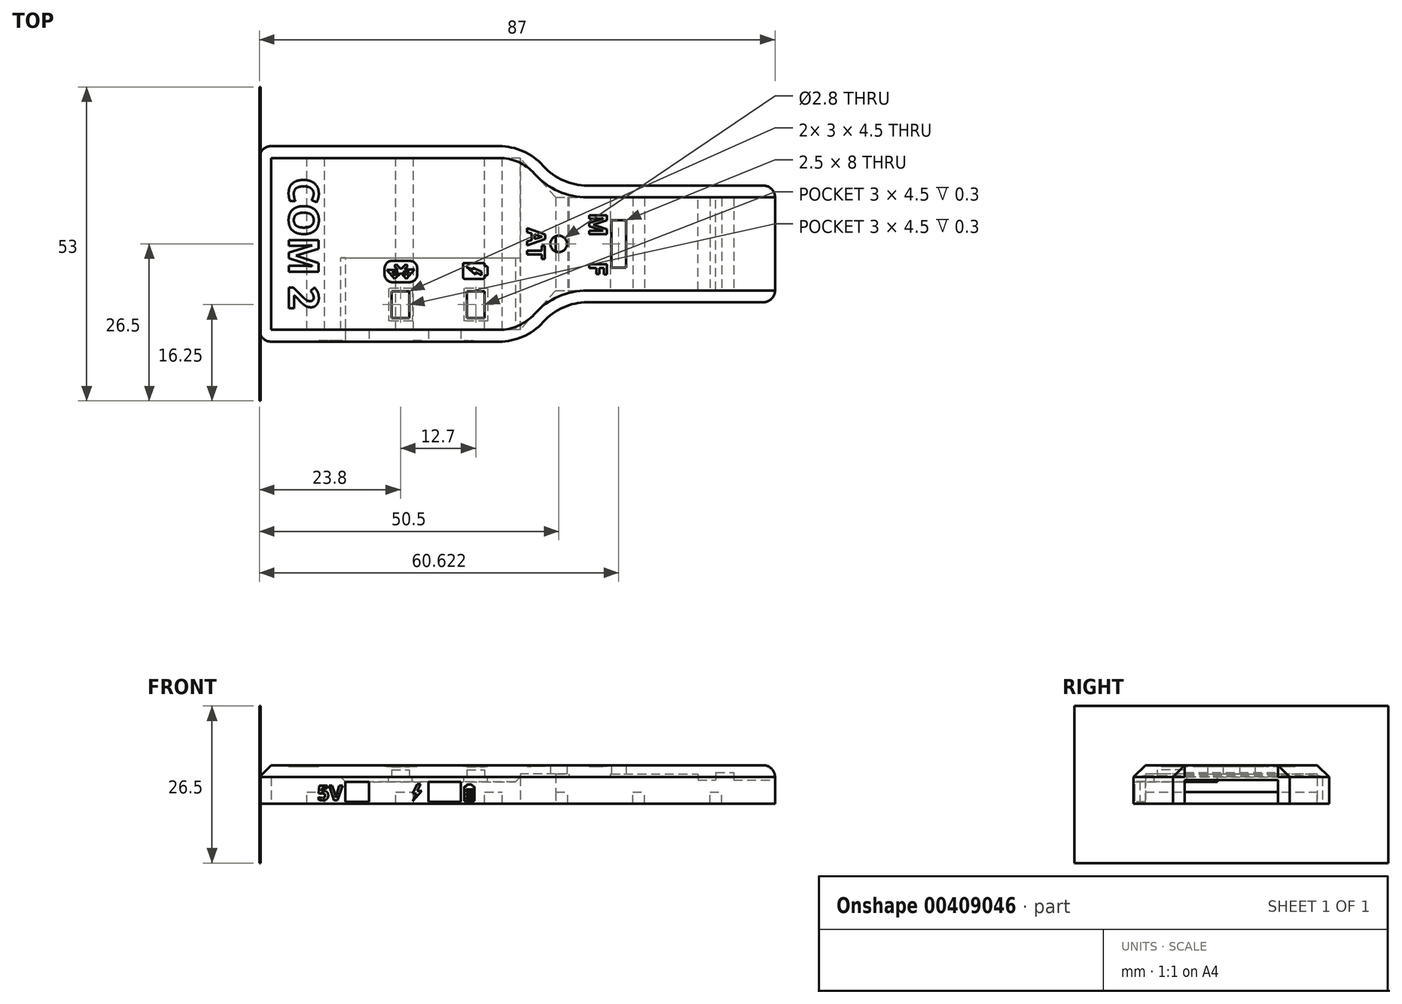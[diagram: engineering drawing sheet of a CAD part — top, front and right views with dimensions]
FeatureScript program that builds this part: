
annotation { "Feature Type Name" : "Feature", "Feature Type Description" : "" }
export const myFeature = defineFeature(function(context is Context, id is Id, definition is map)
    precondition{}
    {
        {
            var Q0;
            Q0=qCreatedBy(makeId("Top.planeOp"),FACE);
            var sketch = newSketch(context, id + "F0", { "sketchPlane" : qUnion([Q0])});
            skLineSegment(sketch, "E0.bottom", {"start": v(0, 14.5) * mm, "end": v(-42, 14.5) * mm});
            skLineSegment(sketch, "E0.top", {"start": v(0, -14.5) * mm, "end": v(-42, -14.5) * mm});
            skLineSegment(sketch, "E0.left", {"start": v(0, 14.5) * mm, "end": v(0, -14.5) * mm});
            skLineSegment(sketch, "E0.right", {"start": v(-42, 14.5) * mm, "end": v(-42, -14.5) * mm});
            skLineSegment(sketch, "E1.bottom", {"start": v(6, 7.85) * mm, "end": v(41, 7.85) * mm});
            skLineSegment(sketch, "E1.top", {"start": v(6, -7.85) * mm, "end": v(41, -7.85) * mm});
            skLineSegment(sketch, "E1.left", {"start": v(6, 7.85) * mm, "end": v(6, -7.85) * mm});
            skLineSegment(sketch, "E1.right", {"start": v(41, 7.85) * mm, "end": v(41, -7.85) * mm});
            skLineSegment(sketch, "E2", {"start": v(6, 7.85) * mm, "end": v(0, 14.5) * mm});
            skLineSegment(sketch, "E3", {"start": v(6, -7.85) * mm, "end": v(0, -14.5) * mm});
            skCircle(sketch, "E4", {"center": v(6.5, 0) * mm, "radius": 1.4 * mm});
            skLineSegment(sketch, "E5.bottom", {"start": v(-29.5, -14.5) * mm, "end": v(-25.5, -14.5) * mm});
            skLineSegment(sketch, "E5.top", {"start": v(-29.5, -17) * mm, "end": v(-25.5, -17) * mm});
            skLineSegment(sketch, "E5.left", {"start": v(-29.5, -14.5) * mm, "end": v(-29.5, -17) * mm});
            skLineSegment(sketch, "E5.right", {"start": v(-25.5, -14.5) * mm, "end": v(-25.5, -17) * mm});
            skLineSegment(sketch, "E6.bottom", {"start": v(-15.5, -14.5) * mm, "end": v(-10, -14.5) * mm});
            skLineSegment(sketch, "E6.top", {"start": v(-15.5, -17) * mm, "end": v(-10, -17) * mm});
            skLineSegment(sketch, "E6.left", {"start": v(-15.5, -14.5) * mm, "end": v(-15.5, -17) * mm});
            skLineSegment(sketch, "E6.right", {"start": v(-10, -14.5) * mm, "end": v(-10, -17) * mm});
            skLineSegment(sketch, "E7.bottom", {"start": v(-21.2, -8.5) * mm, "end": v(-19.2, -8.5) * mm});
            skLineSegment(sketch, "E7.top", {"start": v(-21.2, -12) * mm, "end": v(-19.2, -12) * mm});
            skLineSegment(sketch, "E7.left", {"start": v(-21.2, -8.5) * mm, "end": v(-21.2, -12) * mm});
            skLineSegment(sketch, "E7.right", {"start": v(-19.2, -8.5) * mm, "end": v(-19.2, -12) * mm});
            skLineSegment(sketch, "E8.bottom", {"start": v(-8.5, -8.5) * mm, "end": v(-6.5, -8.5) * mm});
            skLineSegment(sketch, "E8.top", {"start": v(-8.5, -12) * mm, "end": v(-6.5, -12) * mm});
            skLineSegment(sketch, "E8.left", {"start": v(-8.5, -8.5) * mm, "end": v(-8.5, -12) * mm});
            skLineSegment(sketch, "E8.right", {"start": v(-6.5, -8.5) * mm, "end": v(-6.5, -12) * mm});
            skLineSegment(sketch, "E9.bottom", {"start": v(-24.5, -14.5) * mm, "end": v(-30.5, -14.5) * mm});
            skLineSegment(sketch, "E9.top", {"start": v(-24.5, -9.5) * mm, "end": v(-30.5, -9.5) * mm});
            skLineSegment(sketch, "E9.left", {"start": v(-24.5, -14.5) * mm, "end": v(-24.5, -9.5) * mm});
            skLineSegment(sketch, "E9.right", {"start": v(-30.5, -14.5) * mm, "end": v(-30.5, -9.5) * mm});
            skLineSegment(sketch, "E10.bottom", {"start": v(-20, -14.5) * mm, "end": v(-7.5, -14.5) * mm});
            skLineSegment(sketch, "E10.top", {"start": v(-20, -13) * mm, "end": v(-7, -13) * mm});
            skLineSegment(sketch, "E10.left", {"start": v(-20, -14.5) * mm, "end": v(-20, -13) * mm});
            skLineSegment(sketch, "E10.right", {"start": v(-7, -14.5) * mm, "end": v(-7, -13) * mm});
            skLineSegment(sketch, "E11.bottom", {"start": v(8.2, -7.85) * mm, "end": v(15.2, -7.85) * mm});
            skLineSegment(sketch, "E11.top", {"start": v(8.2, 7.85) * mm, "end": v(15.2, 7.85) * mm});
            skLineSegment(sketch, "E11.left", {"start": v(8.2, -7.85) * mm, "end": v(8.2, 7.85) * mm});
            skLineSegment(sketch, "E11.right", {"start": v(15.2, -7.85) * mm, "end": v(15.2, 7.85) * mm});
            skLineSegment(sketch, "E12.bottom", {"start": v(17.87, 4) * mm, "end": v(15.37, 4) * mm});
            skLineSegment(sketch, "E12.top", {"start": v(17.87, -4) * mm, "end": v(15.37, -4) * mm});
            skLineSegment(sketch, "E12.left", {"start": v(17.87, 4) * mm, "end": v(17.87, -4) * mm});
            skLineSegment(sketch, "E12.right", {"start": v(15.37, 4) * mm, "end": v(15.37, -4) * mm});
            skPoint(sketch, "E12.middle", {"position": v(16.62, 0) * mm});
            skLineSegment(sketch, "E13", {"start": v(19, -8) * mm, "end": v(19, 8) * mm});
            skLineSegment(sketch, "E14", {"start": v(30, -7.85) * mm, "end": v(30, 7.85) * mm});
            skLineSegment(sketch, "E15", {"start": v(36, -7.85) * mm, "end": v(36, 7.85) * mm});
            skLineSegment(sketch, "E16", {"start": v(33, -7.85) * mm, "end": v(33, 7.85) * mm});
            skLineSegment(sketch, "E17.0", {"start": v(-9, -12.5) * mm, "end": v(-6, -12.5) * mm});
            skLineSegment(sketch, "E17.1", {"start": v(-9, -8) * mm, "end": v(-9, -12.5) * mm});
            skLineSegment(sketch, "E17.2", {"start": v(-9, -8) * mm, "end": v(-6, -8) * mm});
            skLineSegment(sketch, "E17.3", {"start": v(-6, -8) * mm, "end": v(-6, -12.5) * mm});
            skLineSegment(sketch, "E18.0", {"start": v(-21.7, -12.5) * mm, "end": v(-18.7, -12.5) * mm});
            skLineSegment(sketch, "E18.1", {"start": v(-21.7, -8) * mm, "end": v(-21.7, -12.5) * mm});
            skLineSegment(sketch, "E18.2", {"start": v(-21.7, -8) * mm, "end": v(-18.7, -8) * mm});
            skLineSegment(sketch, "E18.3", {"start": v(-18.7, -8) * mm, "end": v(-18.7, -12.5) * mm});
            skSolve(sketch);
        }
        {
            var Q0;
            Q0=makeQuery(id+"F0.imprint","IMPRINT",FACE,{"disambiguationData":[TD([[makeQuery(id+"F0.imprint","IMPRINT",EDGE,{"derivedFrom":sQuery(id+"F0.wireOp",EDGE,"E0.bottom")}),1.0]])]});
            var Q1;
            Q1=makeQuery(id+"F0.imprint","IMPRINT",FACE,{"disambiguationData":[TD([[makeQuery(id+"F0.imprint","IMPRINT",EDGE,{"derivedFrom":sQuery(id+"F0.wireOp",EDGE,"E9.top")}),1.0]])]});
            var Q2;
            {var subQ0=sQuery(id+"F0.wireOp",EDGE,"E3");Q2=makeQuery(id+"F0.imprint","IMPRINT",FACE,{"disambiguationData":[TD([[makeQuery(id+"F0.imprint","IMPRINT",EDGE,{"derivedFrom":subQ0}),-1.0]])]});}
            var Q3;
            {var subQ0=sQuery(id+"F0.wireOp",EDGE,"E2");Q3=makeQuery(id+"F0.imprint","IMPRINT",FACE,{"disambiguationData":[TD([[makeQuery(id+"F0.imprint","IMPRINT",EDGE,{"derivedFrom":subQ0}),1.0]])]});}
            var Q4;
            Q4=makeQuery(id+"F0.imprint","IMPRINT",FACE,{"disambiguationData":[TD([[makeQuery(id+"F0.imprint","IMPRINT",EDGE,{"derivedFrom":sQuery(id+"F0.wireOp",EDGE,"E10.top")}),-1.0]])]});
            var Q5;
            Q5=makeQuery(id+"F0.imprint","IMPRINT",FACE,{"disambiguationData":[TD([[makeQuery(id+"F0.imprint","IMPRINT",EDGE,{"derivedFrom":sQuery(id+"F0.wireOp",EDGE,"E7.bottom")}),-1.0]])]});
            var Q6;
            Q6=makeQuery(id+"F0.imprint","IMPRINT",FACE,{"disambiguationData":[TD([[makeQuery(id+"F0.imprint","IMPRINT",EDGE,{"derivedFrom":sQuery(id+"F0.wireOp",EDGE,"E7.bottom")}),1.0]])]});
            var Q7;
            Q7=makeQuery(id+"F0.imprint","IMPRINT",FACE,{"disambiguationData":[TD([[makeQuery(id+"F0.imprint","IMPRINT",EDGE,{"derivedFrom":sQuery(id+"F0.wireOp",EDGE,"E8.bottom")}),1.0]])]});
            var Q8;
            Q8=makeQuery(id+"F0.imprint","IMPRINT",FACE,{"disambiguationData":[TD([[makeQuery(id+"F0.imprint","IMPRINT",EDGE,{"derivedFrom":sQuery(id+"F0.wireOp",EDGE,"E8.bottom")}),-1.0]])]});
            extrude(context, id + "F1", {"entities" : qUnion([Q0, Q1, Q2, Q3, Q4, Q5, Q6, Q7, Q8]), "depth" : 4.5 * mm});
        }
        {
            var Q0;
            {var subQ5=sQuery(id+"F0.wireOp",EDGE,"E1.bottom");Q0=makeQuery(id+"F0.imprint","IMPRINT",FACE,{"disambiguationData":[TD([[makeQuery(id+"F0.imprint","IMPRINT",EDGE,{"derivedFrom":subQ5}),-1.0]])]});}
            var Q1;
            {var subQ0=sQuery(id+"F0.wireOp",EDGE,"VPpS5lpm-IVwB-HgLS-dtKc-5THlYFBJEJTK");var subQ1=sQuery(id+"F0.wireOp",EDGE,"E1.left");var subQ2=makeQuery(id+"F0.imprint","INTERSECT",VERTEX,{"disambiguationData":[OD(0.0)],"derivedFrom":[subQ1,subQ0]});Q1=makeQuery(id+"F0.imprint","IMPRINT",FACE,{"disambiguationData":[TD([[makeQuery(id+"F0.imprint","IMPRINT",EDGE,{"disambiguationData":[TD([[subQ2,-1.0]])],"derivedFrom":subQ1}),1.0]])]});}
            var Q2;
            {var subQ0=sQuery(id+"F0.wireOp",EDGE,"E4");var subQ1=sQuery(id+"F0.wireOp",EDGE,"E1.left");var subQ2=makeQuery(id+"F0.imprint","INTERSECT",VERTEX,{"disambiguationData":[OD(0.0)],"derivedFrom":[subQ1,subQ0]});Q2=makeQuery(id+"F0.imprint","IMPRINT",FACE,{"disambiguationData":[TD([[makeQuery(id+"F0.imprint","IMPRINT",EDGE,{"disambiguationData":[TD([[subQ2,-1.0]])],"derivedFrom":subQ1}),1.0]])]});}
            var Q3;
            {var subQ0=sQuery(id+"F0.wireOp",EDGE,"E1.right");Q3=makeQuery(id+"F0.imprint","IMPRINT",FACE,{"disambiguationData":[TD([[makeQuery(id+"F0.imprint","IMPRINT",EDGE,{"derivedFrom":subQ0}),-1.0]])]});}
            var Q4;
            {var subQ1=sQuery(id+"F0.wireOp",EDGE,"E1.left");var subQ4=sQuery(id+"F0.wireOp",EDGE,"VGWTlvGl-73NF-PaTW-xvmp-lA1t04jU08i1");var subQ6=makeQuery(id+"F0.imprint","INTERSECT",VERTEX,{"disambiguationData":[OD(0.0)],"derivedFrom":[subQ1,subQ4]});Q4=makeQuery(id+"F0.imprint","IMPRINT",FACE,{"disambiguationData":[TD([[makeQuery(id+"F0.imprint","IMPRINT",EDGE,{"disambiguationData":[TD([[subQ6,-1.0]])],"derivedFrom":subQ1}),1.0]])]});}
            var Q5;
            {var subQ0=sQuery(id+"F0.wireOp",EDGE,"VGWTlvGl-73NF-PaTW-xvmp-lA1t04jU08i1");var subQ1=sQuery(id+"F0.wireOp",EDGE,"E0.left");var subQ2=makeQuery(id+"F0.imprint","INTERSECT",VERTEX,{"disambiguationData":[OD(0.0)],"derivedFrom":[subQ1,subQ0]});Q5=makeQuery(id+"F0.imprint","IMPRINT",FACE,{"disambiguationData":[TD([[makeQuery(id+"F0.imprint","IMPRINT",EDGE,{"disambiguationData":[TD([[subQ2,-1.0]])],"derivedFrom":subQ1}),-1.0]])]});}
            var Q6;
            {var subQ4=sQuery(id+"F0.wireOp",EDGE,"VGWTlvGl-73NF-PaTW-xvmp-lA1t04jU08i1");var subQ7=sQuery(id+"F0.wireOp",EDGE,"E0.left");var subQ9=makeQuery(id+"F0.imprint","INTERSECT",VERTEX,{"disambiguationData":[OD(0.0)],"derivedFrom":[subQ7,subQ4]});Q6=makeQuery(id+"F0.imprint","IMPRINT",FACE,{"disambiguationData":[TD([[makeQuery(id+"F0.imprint","IMPRINT",EDGE,{"disambiguationData":[TD([[subQ9,-1.0]])],"derivedFrom":subQ7}),1.0]])]});}
            var Q7;
            {var subQ0=sQuery(id+"F0.wireOp",EDGE,"10CGU6lO-faRA-ZIwZ-rcka-2xEhCK4ulN59");var subQ1=sQuery(id+"F0.wireOp",EDGE,"E1.left");var subQ2=makeQuery(id+"F0.imprint","INTERSECT",VERTEX,{"disambiguationData":[OD(0.0)],"derivedFrom":[subQ1,subQ0]});Q7=makeQuery(id+"F0.imprint","IMPRINT",FACE,{"disambiguationData":[TD([[makeQuery(id+"F0.imprint","IMPRINT",EDGE,{"disambiguationData":[TD([[subQ2,-1.0]])],"derivedFrom":subQ1}),-1.0]])]});}
            var Q8;
            {var subQ0=sQuery(id+"F0.wireOp",EDGE,"E4");var subQ1=sQuery(id+"F0.wireOp",EDGE,"E1.left");var subQ2=makeQuery(id+"F0.imprint","INTERSECT",VERTEX,{"disambiguationData":[OD(0.0)],"derivedFrom":[subQ1,subQ0]});Q8=makeQuery(id+"F0.imprint","IMPRINT",FACE,{"disambiguationData":[TD([[makeQuery(id+"F0.imprint","IMPRINT",EDGE,{"disambiguationData":[TD([[subQ2,-1.0]])],"derivedFrom":subQ1}),-1.0]])]});}
            var Q9;
            {var subQ1=sQuery(id+"F0.wireOp",EDGE,"E1.left");var subQ3=sQuery(id+"F0.wireOp",EDGE,"10CGU6lO-faRA-ZIwZ-rcka-2xEhCK4ulN59");var subQ4=makeQuery(id+"F0.imprint","INTERSECT",VERTEX,{"disambiguationData":[OD(0.0)],"derivedFrom":[subQ1,subQ3]});Q9=makeQuery(id+"F0.imprint","IMPRINT",FACE,{"disambiguationData":[TD([[makeQuery(id+"F0.imprint","IMPRINT",EDGE,{"disambiguationData":[TD([[subQ4,1.0]])],"derivedFrom":subQ3}),-1.0]])]});}
            var Q10;
            {var subQ0=sQuery(id+"F0.wireOp",EDGE,"E11.left");var subQ1=sQuery(id+"F0.wireOp",EDGE,"10CGU6lO-faRA-ZIwZ-rcka-2xEhCK4ulN59");var subQ2=makeQuery(id+"F0.imprint","INTERSECT",VERTEX,{"disambiguationData":[OD(0.0)],"derivedFrom":[subQ1,subQ0]});Q10=makeQuery(id+"F0.imprint","IMPRINT",FACE,{"disambiguationData":[TD([[makeQuery(id+"F0.imprint","IMPRINT",EDGE,{"disambiguationData":[TD([[subQ2,1.0]])],"derivedFrom":subQ1}),-1.0]])]});}
            var Q11;
            {var subQ1=sQuery(id+"F0.wireOp",EDGE,"E11.bottom");Q11=makeQuery(id+"F0.imprint","IMPRINT",FACE,{"disambiguationData":[TD([[makeQuery(id+"F0.imprint","IMPRINT",EDGE,{"derivedFrom":subQ1}),1.0]])]});}
            var Q12;
            {var subQ1=sQuery(id+"F0.wireOp",EDGE,"E1.left");var subQ3=sQuery(id+"F0.wireOp",EDGE,"10CGU6lO-faRA-ZIwZ-rcka-2xEhCK4ulN59");var subQ4=makeQuery(id+"F0.imprint","INTERSECT",VERTEX,{"disambiguationData":[OD(1.0)],"derivedFrom":[subQ1,subQ3]});Q12=makeQuery(id+"F0.imprint","IMPRINT",FACE,{"disambiguationData":[TD([[makeQuery(id+"F0.imprint","IMPRINT",EDGE,{"disambiguationData":[TD([[subQ4,-1.0]])],"derivedFrom":subQ3}),-1.0]])]});}
            var Q13;
            {var subQ0=sQuery(id+"F0.wireOp",EDGE,"10CGU6lO-faRA-ZIwZ-rcka-2xEhCK4ulN59");var subQ1=sQuery(id+"F0.wireOp",EDGE,"E1.left");var subQ2=makeQuery(id+"F0.imprint","INTERSECT",VERTEX,{"disambiguationData":[OD(0.0)],"derivedFrom":[subQ1,subQ0]});Q13=makeQuery(id+"F0.imprint","IMPRINT",FACE,{"disambiguationData":[TD([[makeQuery(id+"F0.imprint","IMPRINT",EDGE,{"disambiguationData":[TD([[subQ2,-1.0]])],"derivedFrom":subQ1}),1.0]])]});}
            var Q14;
            {var subQ0=sQuery(id+"F0.wireOp",EDGE,"E11.left");var subQ1=sQuery(id+"F0.wireOp",EDGE,"10CGU6lO-faRA-ZIwZ-rcka-2xEhCK4ulN59");var subQ2=makeQuery(id+"F0.imprint","INTERSECT",VERTEX,{"disambiguationData":[OD(0.0)],"derivedFrom":[subQ1,subQ0]});Q14=makeQuery(id+"F0.imprint","IMPRINT",FACE,{"disambiguationData":[TD([[makeQuery(id+"F0.imprint","IMPRINT",EDGE,{"disambiguationData":[TD([[subQ2,1.0]])],"derivedFrom":subQ1}),1.0]])]});}
            var Q15;
            {var subQ0=sQuery(id+"F0.wireOp",EDGE,"HnFFDSZL-4jIR-ZRKm-03Gk-MsSLVKgGCAKZ");var subQ3=sQuery(id+"F0.wireOp",EDGE,"E11.left");var subQ5=makeQuery(id+"F0.imprint","INTERSECT",VERTEX,{"disambiguationData":[OD(1.0)],"derivedFrom":[subQ0,subQ3]});Q15=makeQuery(id+"F0.imprint","IMPRINT",FACE,{"disambiguationData":[TD([[makeQuery(id+"F0.imprint","IMPRINT",EDGE,{"disambiguationData":[TD([[subQ5,1.0]])],"derivedFrom":subQ3}),1.0]])]});}
            var Q16;
            {var subQ5=sQuery(id+"F0.wireOp",EDGE,"E12.left");Q16=makeQuery(id+"F0.imprint","IMPRINT",FACE,{"disambiguationData":[TD([[makeQuery(id+"F0.imprint","IMPRINT",EDGE,{"derivedFrom":subQ5}),-1.0]])]});}
            var Q17;
            {var subQ5=sQuery(id+"F0.wireOp",EDGE,"E12.right");Q17=makeQuery(id+"F0.imprint","IMPRINT",FACE,{"disambiguationData":[TD([[makeQuery(id+"F0.imprint","IMPRINT",EDGE,{"derivedFrom":subQ5}),1.0]])]});}
            var Q18;
            {var subQ10=sQuery(id+"F0.wireOp",EDGE,"E12.left");Q18=makeQuery(id+"F0.imprint","IMPRINT",FACE,{"disambiguationData":[TD([[makeQuery(id+"F0.imprint","IMPRINT",EDGE,{"derivedFrom":subQ10}),1.0]])]});}
            var Q19;
            {var subQ0=sQuery(id+"F0.wireOp",EDGE,"E13");Q19=makeQuery(id+"F0.imprint","IMPRINT",FACE,{"disambiguationData":[TD([[makeQuery(id+"F0.imprint","IMPRINT",EDGE,{"derivedFrom":subQ0}),-1.0]])]});}
            var Q20;
            {var subQ0=sQuery(id+"F0.wireOp",EDGE,"E14");Q20=makeQuery(id+"F0.imprint","IMPRINT",FACE,{"disambiguationData":[TD([[makeQuery(id+"F0.imprint","IMPRINT",EDGE,{"derivedFrom":subQ0}),-1.0]])]});}
            var Q21;
            {var subQ0=sQuery(id+"F0.wireOp",EDGE,"E15");Q21=makeQuery(id+"F0.imprint","IMPRINT",FACE,{"disambiguationData":[TD([[makeQuery(id+"F0.imprint","IMPRINT",EDGE,{"derivedFrom":subQ0}),1.0]])]});}
            extrude(context, id + "F2", {"entities" : qUnion([Q0, Q1, Q2, Q3, Q4, Q5, Q6, Q7, Q8, Q9, Q10, Q11, Q12, Q13, Q14, Q15, Q16, Q17, Q18, Q19, Q20, Q21]), "depth" : 4.5 * mm});
        }
        {
            var Q0;
            {var subQ0=sQuery(id+"F0.wireOp",EDGE,"VPpS5lpm-IVwB-HgLS-dtKc-5THlYFBJEJTK");var subQ2=sQuery(id+"F0.wireOp",EDGE,"E1.left");var subQ3=makeQuery(id+"F0.imprint","INTERSECT",VERTEX,{"disambiguationData":[OD(0.0)],"derivedFrom":[subQ2,subQ0]});Q0=makeQuery(id+"F0.imprint","IMPRINT",FACE,{"disambiguationData":[TD([[makeQuery(id+"F0.imprint","IMPRINT",EDGE,{"disambiguationData":[TD([[subQ3,-1.0]])],"derivedFrom":subQ2}),-1.0]])]});}
            var Q1;
            {var subQ0=sQuery(id+"F0.wireOp",EDGE,"y9EbTcyz-21YZ-qjv3-pbne-yzflViiAGyzZ");Q1=makeQuery(id+"F0.imprint","IMPRINT",FACE,{"disambiguationData":[TD([[makeQuery(id+"F0.imprint","IMPRINT",EDGE,{"derivedFrom":subQ0}),-1.0]])]});}
            var Q2;
            {var subQ0=sQuery(id+"F0.wireOp",EDGE,"10CGU6lO-faRA-ZIwZ-rcka-2xEhCK4ulN59");var subQ1=sQuery(id+"F0.wireOp",EDGE,"E1.left");var subQ2=makeQuery(id+"F0.imprint","INTERSECT",VERTEX,{"disambiguationData":[OD(0.0)],"derivedFrom":[subQ1,subQ0]});Q2=makeQuery(id+"F0.imprint","IMPRINT",FACE,{"disambiguationData":[TD([[makeQuery(id+"F0.imprint","IMPRINT",EDGE,{"disambiguationData":[TD([[subQ2,-1.0]])],"derivedFrom":subQ1}),-1.0]])]});}
            var Q3;
            {var subQ4=sQuery(id+"F0.wireOp",EDGE,"VGWTlvGl-73NF-PaTW-xvmp-lA1t04jU08i1");var subQ7=sQuery(id+"F0.wireOp",EDGE,"E0.left");var subQ9=makeQuery(id+"F0.imprint","INTERSECT",VERTEX,{"disambiguationData":[OD(0.0)],"derivedFrom":[subQ7,subQ4]});Q3=makeQuery(id+"F0.imprint","IMPRINT",FACE,{"disambiguationData":[TD([[makeQuery(id+"F0.imprint","IMPRINT",EDGE,{"disambiguationData":[TD([[subQ9,-1.0]])],"derivedFrom":subQ7}),1.0]])]});}
            var Q4;
            {var subQ0=sQuery(id+"F0.wireOp",EDGE,"VGWTlvGl-73NF-PaTW-xvmp-lA1t04jU08i1");var subQ1=sQuery(id+"F0.wireOp",EDGE,"E0.left");var subQ2=makeQuery(id+"F0.imprint","INTERSECT",VERTEX,{"disambiguationData":[OD(0.0)],"derivedFrom":[subQ1,subQ0]});Q4=makeQuery(id+"F0.imprint","IMPRINT",FACE,{"disambiguationData":[TD([[makeQuery(id+"F0.imprint","IMPRINT",EDGE,{"disambiguationData":[TD([[subQ2,-1.0]])],"derivedFrom":subQ1}),-1.0]])]});}
            extrude(context, id + "F3", {"entities" : qUnion([Q0, Q1, Q2, Q3, Q4]), "depth" : 4.5 * mm});
        }
        {
            var Q0;
            Q0=makeQuery(id+"F1.opExtrude","SWEPT_BODY",BODY,{"disambiguationData":[OSD([sQuery(id+"F0.wireOp",EDGE,"E0.bottom"),sQuery(id+"F0.wireOp",EDGE,"E0.top"),sQuery(id+"F0.wireOp",EDGE,"E0.right"),sQuery(id+"F0.wireOp",EDGE,"E1.left"),sQuery(id+"F0.wireOp",EDGE,"E2"),sQuery(id+"F0.wireOp",EDGE,"E3"),sQuery(id+"F0.wireOp",EDGE,"E6.bottom"),sQuery(id+"F0.wireOp",EDGE,"E9.bottom"),sQuery(id+"F0.wireOp",EDGE,"VGWTlvGl-73NF-PaTW-xvmp-lA1t04jU08i1")])]});
            var Q1;
            Q1=makeQuery(id+"F2.opExtrude","SWEPT_BODY",BODY,{"disambiguationData":[OSD([sQuery(id+"F0.wireOp",EDGE,"E1.bottom"),sQuery(id+"F0.wireOp",EDGE,"E1.top"),sQuery(id+"F0.wireOp",EDGE,"E1.left"),sQuery(id+"F0.wireOp",EDGE,"E1.right"),sQuery(id+"F0.wireOp",EDGE,"VGWTlvGl-73NF-PaTW-xvmp-lA1t04jU08i1")])]});
            var Q2;
            Q2=makeQuery(id+"F3.opExtrude","SWEPT_BODY",BODY,{"disambiguationData":[OSD([sQuery(id+"F0.wireOp",EDGE,"E1.left"),sQuery(id+"F0.wireOp",EDGE,"E4"),sQuery(id+"F0.wireOp",EDGE,"VGWTlvGl-73NF-PaTW-xvmp-lA1t04jU08i1")])]});
            booleanBodies(context, id + "F4", {"operationType" : BooleanOperationType.UNION, "tools" : qUnion([Q0, Q1, Q2])});
        }
        {
            var Q0;
            {var subQ0=sQuery(id+"F0.wireOp",EDGE,"VGWTlvGl-73NF-PaTW-xvmp-lA1t04jU08i1");var subQ1=sQuery(id+"F0.wireOp",EDGE,"E1.left");Q0=makeQuery(id+"F4.opBoolean","MERGE",FACE,{"derivedFrom":[makeQuery(id+"F1.opExtrude","CAP_FACE",FACE,{"disambiguationData":[OSD([sQuery(id+"F0.wireOp",EDGE,"E0.bottom"),sQuery(id+"F0.wireOp",EDGE,"E0.top"),sQuery(id+"F0.wireOp",EDGE,"E0.right"),subQ1,sQuery(id+"F0.wireOp",EDGE,"E2"),sQuery(id+"F0.wireOp",EDGE,"E3"),sQuery(id+"F0.wireOp",EDGE,"E6.bottom"),sQuery(id+"F0.wireOp",EDGE,"E9.bottom"),subQ0])],"isStart":true}),makeQuery(id+"F2.opExtrude","CAP_FACE",FACE,{"disambiguationData":[OSD([sQuery(id+"F0.wireOp",EDGE,"E1.bottom"),sQuery(id+"F0.wireOp",EDGE,"E1.top"),subQ1,sQuery(id+"F0.wireOp",EDGE,"E1.right"),subQ0])],"isStart":true})]});}
            shell(context, id + "F5", {"entities" : qUnion([Q0]), "thickness" : 2 * mm, "oppositeDirection" : true});
        }
        {
            var Q0;
            {var subQ0=sQuery(id+"F0.wireOp",EDGE,"E4");var subQ1=sQuery(id+"F0.wireOp",EDGE,"E1.left");var subQ2=makeQuery(id+"F0.imprint","INTERSECT",VERTEX,{"disambiguationData":[OD(0.0)],"derivedFrom":[subQ1,subQ0]});Q0=makeQuery(id+"F0.imprint","IMPRINT",FACE,{"disambiguationData":[TD([[makeQuery(id+"F0.imprint","IMPRINT",EDGE,{"disambiguationData":[TD([[subQ2,-1.0]])],"derivedFrom":subQ1}),1.0]])]});}
            var Q1;
            {var subQ0=sQuery(id+"F0.wireOp",EDGE,"E4");var subQ1=sQuery(id+"F0.wireOp",EDGE,"E1.left");var subQ2=makeQuery(id+"F0.imprint","INTERSECT",VERTEX,{"disambiguationData":[OD(0.0)],"derivedFrom":[subQ1,subQ0]});Q1=makeQuery(id+"F0.imprint","IMPRINT",FACE,{"disambiguationData":[TD([[makeQuery(id+"F0.imprint","IMPRINT",EDGE,{"disambiguationData":[TD([[subQ2,-1.0]])],"derivedFrom":subQ1}),-1.0]])]});}
            extrude(context, id + "F6", {"entities" : qUnion([Q0, Q1]), "operationType" : NewBodyOperationType.REMOVE, "depth" : 25 * mm});
        }
        {
            var Q0;
            Q0=makeQuery(id+"F0.imprint","IMPRINT",FACE,{"disambiguationData":[TD([[makeQuery(id+"F0.imprint","IMPRINT",EDGE,{"derivedFrom":sQuery(id+"F0.wireOp",EDGE,"E5.top")}),1.0]])]});
            var Q1;
            Q1=makeQuery(id+"F0.imprint","IMPRINT",FACE,{"disambiguationData":[TD([[makeQuery(id+"F0.imprint","IMPRINT",EDGE,{"derivedFrom":sQuery(id+"F0.wireOp",EDGE,"E6.bottom")}),-1.0]])]});
            var Q2;
            Q2=makeQuery(id+"F0.imprint","IMPRINT",FACE,{"disambiguationData":[TD([[makeQuery(id+"F0.imprint","IMPRINT",EDGE,{"derivedFrom":sQuery(id+"F0.wireOp",EDGE,"E9.top")}),1.0]])]});
            var Q3;
            Q3=makeQuery(id+"F0.imprint","IMPRINT",FACE,{"disambiguationData":[TD([[makeQuery(id+"F0.imprint","IMPRINT",EDGE,{"derivedFrom":sQuery(id+"F0.wireOp",EDGE,"E10.top")}),-1.0]])]});
            var Q4;
            Q4=makeQuery(id+"F0.imprint","IMPRINT",FACE,{"disambiguationData":[TD([[makeQuery(id+"F0.imprint","IMPRINT",EDGE,{"derivedFrom":sQuery(id+"F0.wireOp",EDGE,"E6.top")}),1.0]])]});
            extrude(context, id + "F7", {"entities" : qUnion([Q0, Q1, Q2, Q3, Q4]), "operationType" : NewBodyOperationType.REMOVE, "depth" : 4 * mm});
        }
        {
            var Q0;
            {var subQ0=sQuery(id+"F0.wireOp",EDGE,"HnFFDSZL-4jIR-ZRKm-03Gk-MsSLVKgGCAKZ");var subQ1=sQuery(id+"F0.wireOp",EDGE,"E3");var subQ2=sQuery(id+"F0.wireOp",EDGE,"E1.left");var subQ3=sQuery(id+"F0.wireOp",EDGE,"E1.top");Q0=makeQuery(id+"F4.opBoolean","MERGE",EDGE,{"derivedFrom":[makeQuery(id+"F1.opExtrude","SWEPT_EDGE",EDGE,{"disambiguationData":[OSD([subQ3,subQ2,subQ1,subQ0])]}),makeQuery(id+"F2.opExtrude","SWEPT_EDGE",EDGE,{"disambiguationData":[OSD([subQ3,subQ2,subQ1,subQ0])]})]});}
            var Q1;
            Q1=makeQuery(id+"F1.opExtrude","SWEPT_EDGE",EDGE,{"disambiguationData":[OSD([sQuery(id+"F0.wireOp",EDGE,"E0.top"),sQuery(id+"F0.wireOp",EDGE,"E0.left"),sQuery(id+"F0.wireOp",EDGE,"E3")])]});
            var Q2;
            {var subQ0=sQuery(id+"F0.wireOp",EDGE,"HnFFDSZL-4jIR-ZRKm-03Gk-MsSLVKgGCAKZ");var subQ1=sQuery(id+"F0.wireOp",EDGE,"E2");var subQ2=sQuery(id+"F0.wireOp",EDGE,"E1.left");var subQ3=sQuery(id+"F0.wireOp",EDGE,"E1.bottom");Q2=makeQuery(id+"F4.opBoolean","MERGE",EDGE,{"derivedFrom":[makeQuery(id+"F1.opExtrude","SWEPT_EDGE",EDGE,{"disambiguationData":[OSD([subQ3,subQ2,subQ1,subQ0])]}),makeQuery(id+"F2.opExtrude","SWEPT_EDGE",EDGE,{"disambiguationData":[OSD([subQ3,subQ2,subQ1,subQ0])]})]});}
            var Q3;
            Q3=makeQuery(id+"F1.opExtrude","SWEPT_EDGE",EDGE,{"disambiguationData":[OSD([sQuery(id+"F0.wireOp",EDGE,"E0.bottom"),sQuery(id+"F0.wireOp",EDGE,"E0.left"),sQuery(id+"F0.wireOp",EDGE,"E2")])]});
            fillet(context, id + "F8", {"entities" : qUnion([Q0, Q1, Q2, Q3]), "radius" : 10 * mm, "tangentPropagation" : true, "allowEdgeOverflow" : false});
        }
        {
            var Q0;
            Q0=makeQuery(id+"F5.opShell","OFFSET_FACE",FACE,{"disambiguationData":[OSD([sQuery(id+"F0.wireOp",EDGE,"E1.right")])]});
            extrude(context, id + "F9", {"entities" : qUnion([Q0]), "operationType" : NewBodyOperationType.REMOVE, "oppositeDirection" : true, "depth" : 25 * mm});
        }
        {
            var Q0;
            Q0=makeQuery(id+"F1.opExtrude","SWEPT_EDGE",EDGE,{"disambiguationData":[OSD([sQuery(id+"F0.wireOp",EDGE,"E0.bottom"),sQuery(id+"F0.wireOp",EDGE,"E0.right")])]});
            var Q1;
            Q1=makeQuery(id+"F1.opExtrude","SWEPT_EDGE",EDGE,{"disambiguationData":[OSD([sQuery(id+"F0.wireOp",EDGE,"E0.top"),sQuery(id+"F0.wireOp",EDGE,"E0.right")])]});
            fillet(context, id + "F10", {"entities" : qUnion([Q0, Q1]), "radius" : 2 * mm, "tangentPropagation" : true, "allowEdgeOverflow" : false});
        }
        {
            var Q0;
            {var subQ0=sQuery(id+"F0.wireOp",EDGE,"HnFFDSZL-4jIR-ZRKm-03Gk-MsSLVKgGCAKZ");var subQ7=sQuery(id+"F0.wireOp",EDGE,"E0.left");var subQ8=makeQuery(id+"F0.imprint","INTERSECT",VERTEX,{"disambiguationData":[OD(0.0)],"derivedFrom":[subQ7,subQ0]});Q0=makeQuery(id+"F0.imprint","IMPRINT",FACE,{"disambiguationData":[TD([[makeQuery(id+"F0.imprint","IMPRINT",EDGE,{"disambiguationData":[TD([[subQ8,-1.0]])],"derivedFrom":subQ7}),1.0]])]});}
            var Q1;
            {var subQ0=sQuery(id+"F0.wireOp",EDGE,"10CGU6lO-faRA-ZIwZ-rcka-2xEhCK4ulN59");var subQ1=sQuery(id+"F0.wireOp",EDGE,"E1.left");var subQ2=makeQuery(id+"F0.imprint","INTERSECT",VERTEX,{"disambiguationData":[OD(0.0)],"derivedFrom":[subQ1,subQ0]});Q1=makeQuery(id+"F0.imprint","IMPRINT",FACE,{"disambiguationData":[TD([[makeQuery(id+"F0.imprint","IMPRINT",EDGE,{"disambiguationData":[TD([[subQ2,-1.0]])],"derivedFrom":subQ1}),-1.0]])]});}
            var Q2;
            {var subQ0=sQuery(id+"F0.wireOp",EDGE,"10CGU6lO-faRA-ZIwZ-rcka-2xEhCK4ulN59");var subQ1=sQuery(id+"F0.wireOp",EDGE,"E1.left");var subQ2=makeQuery(id+"F0.imprint","INTERSECT",VERTEX,{"disambiguationData":[OD(0.0)],"derivedFrom":[subQ1,subQ0]});Q2=makeQuery(id+"F0.imprint","IMPRINT",FACE,{"disambiguationData":[TD([[makeQuery(id+"F0.imprint","IMPRINT",EDGE,{"disambiguationData":[TD([[subQ2,-1.0]])],"derivedFrom":subQ1}),1.0]])]});}
            var Q3;
            {var subQ1=sQuery(id+"F0.wireOp",EDGE,"E1.left");var subQ3=sQuery(id+"F0.wireOp",EDGE,"10CGU6lO-faRA-ZIwZ-rcka-2xEhCK4ulN59");var subQ4=makeQuery(id+"F0.imprint","INTERSECT",VERTEX,{"disambiguationData":[OD(0.0)],"derivedFrom":[subQ1,subQ3]});Q3=makeQuery(id+"F0.imprint","IMPRINT",FACE,{"disambiguationData":[TD([[makeQuery(id+"F0.imprint","IMPRINT",EDGE,{"disambiguationData":[TD([[subQ4,1.0]])],"derivedFrom":subQ3}),-1.0]])]});}
            var Q4;
            {var subQ1=sQuery(id+"F0.wireOp",EDGE,"E1.left");var subQ3=sQuery(id+"F0.wireOp",EDGE,"10CGU6lO-faRA-ZIwZ-rcka-2xEhCK4ulN59");var subQ4=makeQuery(id+"F0.imprint","INTERSECT",VERTEX,{"disambiguationData":[OD(1.0)],"derivedFrom":[subQ1,subQ3]});Q4=makeQuery(id+"F0.imprint","IMPRINT",FACE,{"disambiguationData":[TD([[makeQuery(id+"F0.imprint","IMPRINT",EDGE,{"disambiguationData":[TD([[subQ4,-1.0]])],"derivedFrom":subQ3}),-1.0]])]});}
            var Q5;
            {var subQ0=sQuery(id+"F0.wireOp",EDGE,"E11.left");var subQ1=sQuery(id+"F0.wireOp",EDGE,"10CGU6lO-faRA-ZIwZ-rcka-2xEhCK4ulN59");var subQ2=makeQuery(id+"F0.imprint","INTERSECT",VERTEX,{"disambiguationData":[OD(0.0)],"derivedFrom":[subQ1,subQ0]});Q5=makeQuery(id+"F0.imprint","IMPRINT",FACE,{"disambiguationData":[TD([[makeQuery(id+"F0.imprint","IMPRINT",EDGE,{"disambiguationData":[TD([[subQ2,1.0]])],"derivedFrom":subQ1}),1.0]])]});}
            var Q6;
            {var subQ0=sQuery(id+"F0.wireOp",EDGE,"E11.left");var subQ1=sQuery(id+"F0.wireOp",EDGE,"10CGU6lO-faRA-ZIwZ-rcka-2xEhCK4ulN59");var subQ2=makeQuery(id+"F0.imprint","INTERSECT",VERTEX,{"disambiguationData":[OD(0.0)],"derivedFrom":[subQ1,subQ0]});Q6=makeQuery(id+"F0.imprint","IMPRINT",FACE,{"disambiguationData":[TD([[makeQuery(id+"F0.imprint","IMPRINT",EDGE,{"disambiguationData":[TD([[subQ2,1.0]])],"derivedFrom":subQ1}),-1.0]])]});}
            extrude(context, id + "F11", {"entities" : qUnion([Q0, Q1, Q2, Q3, Q4, Q5, Q6]), "operationType" : NewBodyOperationType.REMOVE, "depth" : 5 * mm});
        }
        {
            var Q0;
            {var subQ0=sQuery(id+"F0.wireOp",EDGE,"E11.left");var subQ1=sQuery(id+"F0.wireOp",EDGE,"10CGU6lO-faRA-ZIwZ-rcka-2xEhCK4ulN59");var subQ2=makeQuery(id+"F0.imprint","INTERSECT",VERTEX,{"disambiguationData":[OD(0.0)],"derivedFrom":[subQ1,subQ0]});Q0=makeQuery(id+"F0.imprint","IMPRINT",FACE,{"disambiguationData":[TD([[makeQuery(id+"F0.imprint","IMPRINT",EDGE,{"disambiguationData":[TD([[subQ2,1.0]])],"derivedFrom":subQ1}),1.0]])]});}
            var Q1;
            {var subQ10=sQuery(id+"F0.wireOp",EDGE,"E12.left");Q1=makeQuery(id+"F0.imprint","IMPRINT",FACE,{"disambiguationData":[TD([[makeQuery(id+"F0.imprint","IMPRINT",EDGE,{"derivedFrom":subQ10}),1.0]])]});}
            var Q2;
            {var subQ1=sQuery(id+"F0.wireOp",EDGE,"E11.bottom");Q2=makeQuery(id+"F0.imprint","IMPRINT",FACE,{"disambiguationData":[TD([[makeQuery(id+"F0.imprint","IMPRINT",EDGE,{"derivedFrom":subQ1}),1.0]])]});}
            var Q3;
            {var subQ5=sQuery(id+"F0.wireOp",EDGE,"E12.right");Q3=makeQuery(id+"F0.imprint","IMPRINT",FACE,{"disambiguationData":[TD([[makeQuery(id+"F0.imprint","IMPRINT",EDGE,{"derivedFrom":subQ5}),1.0]])]});}
            var Q4;
            {var subQ0=sQuery(id+"F0.wireOp",EDGE,"HnFFDSZL-4jIR-ZRKm-03Gk-MsSLVKgGCAKZ");var subQ3=sQuery(id+"F0.wireOp",EDGE,"E11.left");var subQ5=makeQuery(id+"F0.imprint","INTERSECT",VERTEX,{"disambiguationData":[OD(1.0)],"derivedFrom":[subQ0,subQ3]});Q4=makeQuery(id+"F0.imprint","IMPRINT",FACE,{"disambiguationData":[TD([[makeQuery(id+"F0.imprint","IMPRINT",EDGE,{"disambiguationData":[TD([[subQ5,1.0]])],"derivedFrom":subQ3}),1.0]])]});}
            var Q5;
            {var subQ0=sQuery(id+"F0.wireOp",EDGE,"HnFFDSZL-4jIR-ZRKm-03Gk-MsSLVKgGCAKZ");var subQ3=sQuery(id+"F0.wireOp",EDGE,"E11.left");var subQ5=makeQuery(id+"F0.imprint","INTERSECT",VERTEX,{"disambiguationData":[OD(0.0)],"derivedFrom":[subQ0,subQ3]});Q5=makeQuery(id+"F0.imprint","IMPRINT",FACE,{"disambiguationData":[TD([[makeQuery(id+"F0.imprint","IMPRINT",EDGE,{"disambiguationData":[TD([[subQ5,-1.0]])],"derivedFrom":subQ3}),1.0]])]});}
            var Q6;
            {var subQ0=sQuery(id+"F0.wireOp",EDGE,"E11.left");var subQ1=sQuery(id+"F0.wireOp",EDGE,"10CGU6lO-faRA-ZIwZ-rcka-2xEhCK4ulN59");var subQ2=makeQuery(id+"F0.imprint","INTERSECT",VERTEX,{"disambiguationData":[OD(0.0)],"derivedFrom":[subQ1,subQ0]});Q6=makeQuery(id+"F0.imprint","IMPRINT",FACE,{"disambiguationData":[TD([[makeQuery(id+"F0.imprint","IMPRINT",EDGE,{"disambiguationData":[TD([[subQ2,1.0]])],"derivedFrom":subQ1}),-1.0]])]});}
            extrude(context, id + "F12", {"entities" : qUnion([Q0, Q1, Q2, Q3, Q4, Q5, Q6]), "operationType" : NewBodyOperationType.REMOVE, "depth" : 5 * mm});
        }
        {
            var Q0;
            {var subQ5=sQuery(id+"F0.wireOp",EDGE,"E12.left");Q0=makeQuery(id+"F0.imprint","IMPRINT",FACE,{"disambiguationData":[TD([[makeQuery(id+"F0.imprint","IMPRINT",EDGE,{"derivedFrom":subQ5}),-1.0]])]});}
            extrude(context, id + "F13", {"entities" : qUnion([Q0]), "operationType" : NewBodyOperationType.REMOVE, "depth" : 25 * mm});
        }
        {
            var Q0;
            {var subQ0=sQuery(id+"F0.wireOp",EDGE,"E15");Q0=makeQuery(id+"F0.imprint","IMPRINT",FACE,{"disambiguationData":[TD([[makeQuery(id+"F0.imprint","IMPRINT",EDGE,{"derivedFrom":subQ0}),1.0]])]});}
            var Q1;
            {var subQ0=sQuery(id+"F0.wireOp",EDGE,"E13");Q1=makeQuery(id+"F0.imprint","IMPRINT",FACE,{"disambiguationData":[TD([[makeQuery(id+"F0.imprint","IMPRINT",EDGE,{"derivedFrom":subQ0}),-1.0]])]});}
            extrude(context, id + "F14", {"entities" : qUnion([Q0, Q1]), "operationType" : NewBodyOperationType.REMOVE, "depth" : 5 * mm});
        }
        {
            var Q0;
            {var subQ0=sQuery(id+"F0.wireOp",EDGE,"HnFFDSZL-4jIR-ZRKm-03Gk-MsSLVKgGCAKZ");Q0=makeQuery(id+"F4.opBoolean","MERGE",FACE,{"derivedFrom":[makeQuery(id+"F1.opExtrude","CAP_FACE",FACE,{"disambiguationData":[OSD([sQuery(id+"F0.wireOp",EDGE,"E0.bottom"),sQuery(id+"F0.wireOp",EDGE,"E0.top"),sQuery(id+"F0.wireOp",EDGE,"E0.right"),sQuery(id+"F0.wireOp",EDGE,"E2"),sQuery(id+"F0.wireOp",EDGE,"E3"),sQuery(id+"F0.wireOp",EDGE,"E9.bottom"),sQuery(id+"F0.wireOp",EDGE,"E10.bottom"),subQ0])],"isStart":false}),makeQuery(id+"F2.opExtrude","CAP_FACE",FACE,{"disambiguationData":[OSD([sQuery(id+"F0.wireOp",EDGE,"E1.bottom"),sQuery(id+"F0.wireOp",EDGE,"E1.top"),sQuery(id+"F0.wireOp",EDGE,"E1.right"),subQ0,sQuery(id+"F0.wireOp",EDGE,"E11.bottom"),sQuery(id+"F0.wireOp",EDGE,"E11.top")])],"isStart":false})]});}
            var sketch = newSketch(context, id + "F15", { "sketchPlane" : qUnion([Q0])});
            skPoint(sketch, "E19.middle", {"position": v(-19.64, -4.61) * mm});
            skLineSegment(sketch, "E20", {"start": v(-18.72, -4.71) * mm, "end": v(-19.8, -4.73) * mm});
            skLineSegment(sketch, "E21", {"start": v(-19.8, -4.73) * mm, "end": v(-19.22, -5.28) * mm});
            skLineSegment(sketch, "E22", {"start": v(-19.22, -5.28) * mm, "end": v(-18.72, -4.71) * mm});
            skLineSegment(sketch, "E23", {"start": v(-20.54, -4.76) * mm, "end": v(-21.66, -4.76) * mm});
            skLineSegment(sketch, "E24", {"start": v(-21.66, -4.76) * mm, "end": v(-21.13, -5.31) * mm});
            skLineSegment(sketch, "E25", {"start": v(-21.13, -5.31) * mm, "end": v(-20.54, -4.76) * mm});
            skLineSegment(sketch, "E26", {"start": v(-20.12, -4.91) * mm, "end": v(-21.19, -5.94) * mm});
            skLineSegment(sketch, "E27", {"start": v(-21.19, -5.94) * mm, "end": v(-22.52, -4.36) * mm});
            skLineSegment(sketch, "E28", {"start": v(-22.52, -4.36) * mm, "end": v(-20.6, -4.37) * mm});
            skLineSegment(sketch, "E29", {"start": v(-20.6, -4.37) * mm, "end": v(-21.24, -3.74) * mm});
            skLineSegment(sketch, "E30", {"start": v(-21.24, -3.74) * mm, "end": v(-20.95, -3.45) * mm});
            skLineSegment(sketch, "E31", {"start": v(-20.95, -3.45) * mm, "end": v(-20.1, -4.28) * mm});
            skLineSegment(sketch, "E32", {"start": v(-20.1, -4.28) * mm, "end": v(-19.28, -3.45) * mm});
            skLineSegment(sketch, "E33", {"start": v(-19.28, -3.45) * mm, "end": v(-18.97, -3.75) * mm});
            skLineSegment(sketch, "E34", {"start": v(-18.97, -3.75) * mm, "end": v(-19.56, -4.34) * mm});
            skLineSegment(sketch, "E35", {"start": v(-19.56, -4.34) * mm, "end": v(-17.84, -4.33) * mm});
            skLineSegment(sketch, "E36", {"start": v(-17.84, -4.33) * mm, "end": v(-19.2, -5.89) * mm});
            skLineSegment(sketch, "E37", {"start": v(-19.2, -5.89) * mm, "end": v(-20.12, -4.91) * mm});
            skText(sketch, "E38", { "text": "M    F", "fontName": "OpenSans-Bold.ttf"});
            skText(sketch, "E39", { "text": "AT", "fontName": "OpenSans-Bold.ttf"});
            skText(sketch, "E40", { "text": "COM 2", "fontName": "OpenSans-Bold.ttf"});
            skLineSegment(sketch, "E41.bottom", {"start": v(-6.24, -3.21) * mm, "end": v(-9.4, -3.21) * mm});
            skLineSegment(sketch, "E41.top", {"start": v(-6.24, -5.9) * mm, "end": v(-9.4, -5.9) * mm});
            skLineSegment(sketch, "E41.left", {"start": v(-6, -3.44) * mm, "end": v(-6, -5.66) * mm});
            skLineSegment(sketch, "E41.right", {"start": v(-9.63, -3.44) * mm, "end": v(-9.63, -5.66) * mm});
            skPoint(sketch, "E42.visualSharp", {"position": v(-6, -3.21) * mm});
            skArc(sketch, "E42.filletArc", {"start": v(-6, -3.44) * mm, "mid": v(-6.07, -3.28) * mm, "end": v(-6.24, -3.21) * mm});
            skPoint(sketch, "E43.visualSharp", {"position": v(-6, -5.9) * mm});
            skArc(sketch, "E43.filletArc", {"start": v(-6.24, -5.9) * mm, "mid": v(-6.07, -5.83) * mm, "end": v(-6, -5.66) * mm});
            skPoint(sketch, "E44.visualSharp", {"position": v(-9.63, -3.21) * mm});
            skArc(sketch, "E44.filletArc", {"start": v(-9.4, -3.21) * mm, "mid": v(-9.56, -3.28) * mm, "end": v(-9.63, -3.44) * mm});
            skPoint(sketch, "E45.visualSharp", {"position": v(-9.63, -5.9) * mm});
            skArc(sketch, "E45.filletArc", {"start": v(-9.63, -5.66) * mm, "mid": v(-9.56, -5.83) * mm, "end": v(-9.4, -5.9) * mm});
            skLineSegment(sketch, "E46.bottom", {"start": v(-6, -3.76) * mm, "end": v(-5.74, -3.76) * mm});
            skLineSegment(sketch, "E46.top", {"start": v(-6, -5.35) * mm, "end": v(-5.74, -5.35) * mm});
            skLineSegment(sketch, "E46.left", {"start": v(-6, -3.76) * mm, "end": v(-6, -5.35) * mm});
            skLineSegment(sketch, "E46.right", {"start": v(-5.5, -4) * mm, "end": v(-5.5, -5.11) * mm});
            skPoint(sketch, "E47.visualSharp", {"position": v(-5.5, -3.76) * mm});
            skArc(sketch, "E47.filletArc", {"start": v(-5.5, -4) * mm, "mid": v(-5.57, -3.83) * mm, "end": v(-5.74, -3.76) * mm});
            skPoint(sketch, "E48.visualSharp", {"position": v(-5.5, -5.35) * mm});
            skArc(sketch, "E48.filletArc", {"start": v(-5.74, -5.35) * mm, "mid": v(-5.57, -5.28) * mm, "end": v(-5.5, -5.11) * mm});
            skLineSegment(sketch, "E49", {"start": v(-6.53, -4.71) * mm, "end": v(-7.98, -4) * mm});
            skLineSegment(sketch, "E50", {"start": v(-7.98, -4) * mm, "end": v(-7.98, -4.4) * mm});
            skLineSegment(sketch, "E51", {"start": v(-7.98, -4.4) * mm, "end": v(-9.07, -3.9) * mm});
            skLineSegment(sketch, "E52", {"start": v(-9.07, -3.9) * mm, "end": v(-7.5, -5.2) * mm});
            skLineSegment(sketch, "E53", {"start": v(-7.5, -5.2) * mm, "end": v(-7.5, -4.76) * mm});
            skLineSegment(sketch, "E54", {"start": v(-7.5, -4.76) * mm, "end": v(-6.53, -5.25) * mm});
            skLineSegment(sketch, "E55", {"start": v(-6.53, -5.25) * mm, "end": v(-6.53, -4.71) * mm});
            skLineSegment(sketch, "E56.bottom", {"start": v(-21.54, -6.47) * mm, "end": v(-18.7, -6.47) * mm});
            skLineSegment(sketch, "E56.top", {"start": v(-21.54, -2.84) * mm, "end": v(-18.7, -2.84) * mm});
            skLineSegment(sketch, "E56.left", {"start": v(-22.89, -5.12) * mm, "end": v(-22.89, -4.19) * mm});
            skLineSegment(sketch, "E56.right", {"start": v(-17.35, -5.12) * mm, "end": v(-17.35, -4.19) * mm});
            skPoint(sketch, "E56.middle", {"position": v(-20.12, -4.65) * mm});
            skPoint(sketch, "E57.visualSharp", {"position": v(-17.35, -2.84) * mm});
            skArc(sketch, "E57.filletArc", {"start": v(-17.35, -4.19) * mm, "mid": v(-17.75, -3.23) * mm, "end": v(-18.7, -2.84) * mm});
            skPoint(sketch, "E58.visualSharp", {"position": v(-17.35, -6.47) * mm});
            skArc(sketch, "E58.filletArc", {"start": v(-18.7, -6.47) * mm, "mid": v(-17.75, -6.07) * mm, "end": v(-17.35, -5.12) * mm});
            skPoint(sketch, "E59.visualSharp", {"position": v(-22.89, -6.47) * mm});
            skArc(sketch, "E59.filletArc", {"start": v(-22.89, -5.12) * mm, "mid": v(-22.5, -6.07) * mm, "end": v(-21.54, -6.47) * mm});
            skPoint(sketch, "E60.visualSharp", {"position": v(-22.89, -2.84) * mm});
            skArc(sketch, "E60.filletArc", {"start": v(-21.54, -2.84) * mm, "mid": v(-22.5, -3.23) * mm, "end": v(-22.89, -4.19) * mm});
            const initialGuessF15  = {"E38": [0.01167, 0.0052, 0, -1, 0.003], "E39": [0.0012, 0.00264, 0, -1, 0.003], "E40": [-0.039, 0.0112, 0, -1, 0.005]};
            skSetInitialGuess(sketch, initialGuessF15);
            skSolve(sketch);
        }
        {
            var Q0;
            {var subQ5=sQuery(id+"F15.wireOp",EDGE,"E19.right");Q0=makeQuery(id+"F15.imprint","IMPRINT",FACE,{"disambiguationData":[TD([[makeQuery(id+"F15.imprint","IMPRINT",EDGE,{"derivedFrom":subQ5}),1.0]])]});}
            var Q1;
            {var subQ0=sQuery(id+"F15.wireOp",EDGE,"E19.top");var subQ1=sQuery(id+"F15.wireOp",EDGE,"FoTjqakA-3Q0D-e8Zx-aRf2-kQgUUboiUMlV");var subQ2=makeQuery(id+"F15.imprint","INTERSECT",VERTEX,{"derivedFrom":[subQ1,subQ0]});Q1=makeQuery(id+"F15.imprint","IMPRINT",FACE,{"disambiguationData":[TD([[makeQuery(id+"F15.imprint","IMPRINT",EDGE,{"disambiguationData":[TD([[subQ2,1.0]])],"derivedFrom":subQ1}),-1.0]])]});}
            var Q2;
            {var subQ5=sQuery(id+"F15.wireOp",EDGE,"E19.left");Q2=makeQuery(id+"F15.imprint","IMPRINT",FACE,{"disambiguationData":[TD([[makeQuery(id+"F15.imprint","IMPRINT",EDGE,{"derivedFrom":subQ5}),-1.0]])]});}
            var Q3;
            {var subQ0=sQuery(id+"F15.wireOp",EDGE,"1H3nl5ng-9DyI-yJWU-6AWz-InJrUK3OAsY4");Q3=makeQuery(id+"F15.imprint","IMPRINT",FACE,{"disambiguationData":[TD([[makeQuery(id+"F15.imprint","IMPRINT",EDGE,{"derivedFrom":subQ0}),-1.0]])]});}
            var Q4;
            Q4=makeQuery(id+"F15.imprint","IMPRINT",FACE,{"disambiguationData":[TD([[makeQuery(id+"F15.imprint","IMPRINT",EDGE,{"derivedFrom":sQuery(id+"F15.wireOp",EDGE,"tPRg0zax-F67y-5KnP-cIeF-lg8p1GO7OnOK")}),-1.0]])]});
            var Q5;
            Q5=makeQuery(id+"F15.imprint","IMPRINT",FACE,{"disambiguationData":[TD([[makeQuery(id+"F15.imprint","IMPRINT",EDGE,{"derivedFrom":sQuery(id+"F15.wireOp",EDGE,"E39.sketch_text.stroke-0")}),-1.0]])]});
            var Q6;
            Q6=makeQuery(id+"F15.imprint","IMPRINT",FACE,{"disambiguationData":[TD([[makeQuery(id+"F15.imprint","IMPRINT",EDGE,{"derivedFrom":sQuery(id+"F15.wireOp",EDGE,"E39.sketch_text.stroke-13")}),-1.0]])]});
            var Q7;
            Q7=makeQuery(id+"F15.imprint","IMPRINT",FACE,{"disambiguationData":[TD([[makeQuery(id+"F15.imprint","IMPRINT",EDGE,{"derivedFrom":sQuery(id+"F15.wireOp",EDGE,"E38.sketch_text.stroke-18")}),-1.0]])]});
            var Q8;
            Q8=makeQuery(id+"F15.imprint","IMPRINT",FACE,{"disambiguationData":[TD([[makeQuery(id+"F15.imprint","IMPRINT",EDGE,{"derivedFrom":sQuery(id+"F15.wireOp",EDGE,"E38.sketch_text.stroke-0")}),-1.0]])]});
            var Q9;
            Q9=makeQuery(id+"F15.imprint","IMPRINT",FACE,{"disambiguationData":[TD([[makeQuery(id+"F15.imprint","IMPRINT",EDGE,{"derivedFrom":sQuery(id+"F15.wireOp",EDGE,"E38.sketch_text.stroke-19")}),-1.0]])]});
            var Q10;
            Q10=makeQuery(id+"F15.imprint","IMPRINT",FACE,{"disambiguationData":[TD([[makeQuery(id+"F15.imprint","IMPRINT",EDGE,{"derivedFrom":sQuery(id+"F15.wireOp",EDGE,"E46.bottom")}),-1.0]])]});
            var Q11;
            Q11=makeQuery(id+"F15.imprint","IMPRINT",FACE,{"disambiguationData":[TD([[makeQuery(id+"F15.imprint","IMPRINT",EDGE,{"derivedFrom":sQuery(id+"F15.wireOp",EDGE,"E41.bottom")}),1.0]])]});
            var Q12;
            Q12=makeQuery(id+"F15.imprint","IMPRINT",FACE,{"disambiguationData":[TD([[makeQuery(id+"F15.imprint","IMPRINT",EDGE,{"derivedFrom":sQuery(id+"F15.wireOp",EDGE,"E23")}),1.0]])]});
            var Q13;
            Q13=makeQuery(id+"F15.imprint","IMPRINT",FACE,{"disambiguationData":[TD([[makeQuery(id+"F15.imprint","IMPRINT",EDGE,{"derivedFrom":sQuery(id+"F15.wireOp",EDGE,"E20")}),1.0]])]});
            var Q14;
            Q14=makeQuery(id+"F15.imprint","IMPRINT",FACE,{"disambiguationData":[TD([[makeQuery(id+"F15.imprint","IMPRINT",EDGE,{"derivedFrom":sQuery(id+"F15.wireOp",EDGE,"E26")}),1.0]])]});
            extrude(context, id + "F16", {"entities" : qUnion([Q0, Q1, Q2, Q3, Q4, Q5, Q6, Q7, Q8, Q9, Q10, Q11, Q12, Q13, Q14]), "operationType" : NewBodyOperationType.REMOVE, "oppositeDirection" : true, "depth" : 0.2 * mm});
        }
        {
            var Q0;
            Q0=makeQuery(id+"F2.opExtrude","CAP_EDGE",EDGE,{"disambiguationData":[OSD([sQuery(id+"F0.wireOp",EDGE,"E1.right")])],"isStart":false});
            var Q1;
            Q1=makeQuery(id+"F2.opExtrude","SWEPT_EDGE",EDGE,{"disambiguationData":[OSD([sQuery(id+"F0.wireOp",EDGE,"E1.top"),sQuery(id+"F0.wireOp",EDGE,"E1.right")])]});
            var Q2;
            Q2=makeQuery(id+"F2.opExtrude","SWEPT_EDGE",EDGE,{"disambiguationData":[OSD([sQuery(id+"F0.wireOp",EDGE,"E1.bottom"),sQuery(id+"F0.wireOp",EDGE,"E1.right")])]});
            fillet(context, id + "F17", {"entities" : qUnion([Q0, Q1, Q2]), "radius" : 2 * mm, "tangentPropagation" : true, "allowEdgeOverflow" : false});
        }
        {
            var Q0;
            Q0=makeQuery(id+"F2.opExtrude","CAP_EDGE",EDGE,{"disambiguationData":[OSD([sQuery(id+"F0.wireOp",EDGE,"E1.top"),sQuery(id+"F0.wireOp",EDGE,"E11.bottom")])],"isStart":false});
            var Q1;
            Q1=makeQuery(id+"F2.opExtrude","CAP_EDGE",EDGE,{"disambiguationData":[OSD([sQuery(id+"F0.wireOp",EDGE,"E1.bottom"),sQuery(id+"F0.wireOp",EDGE,"E11.top")])],"isStart":false});
            chamfer(context, id + "F18", {"entities" : qUnion([Q0, Q1]), "width" : 2 * mm, "tangentPropagation" : true});
        }
        {
            var Q0;
            Q0=makeQuery(id+"F0.imprint","IMPRINT",FACE,{"disambiguationData":[TD([[makeQuery(id+"F0.imprint","IMPRINT",EDGE,{"derivedFrom":sQuery(id+"F0.wireOp",EDGE,"E7.bottom")}),-1.0]])]});
            var Q1;
            Q1=makeQuery(id+"F0.imprint","IMPRINT",FACE,{"disambiguationData":[TD([[makeQuery(id+"F0.imprint","IMPRINT",EDGE,{"derivedFrom":sQuery(id+"F0.wireOp",EDGE,"E7.bottom")}),1.0]])]});
            var Q2;
            Q2=makeQuery(id+"F0.imprint","IMPRINT",FACE,{"disambiguationData":[TD([[makeQuery(id+"F0.imprint","IMPRINT",EDGE,{"derivedFrom":sQuery(id+"F0.wireOp",EDGE,"E8.bottom")}),1.0]])]});
            var Q3;
            Q3=makeQuery(id+"F0.imprint","IMPRINT",FACE,{"disambiguationData":[TD([[makeQuery(id+"F0.imprint","IMPRINT",EDGE,{"derivedFrom":sQuery(id+"F0.wireOp",EDGE,"E8.bottom")}),-1.0]])]});
            extrude(context, id + "F19", {"entities" : qUnion([Q0, Q1, Q2, Q3]), "operationType" : NewBodyOperationType.REMOVE, "endBound" : BoundingType.THROUGH_ALL, "depth" : 25 * mm});
        }
        {
            var Q0;
            Q0=makeQuery(id+"F0.imprint","IMPRINT",FACE,{"disambiguationData":[TD([[makeQuery(id+"F0.imprint","IMPRINT",EDGE,{"derivedFrom":sQuery(id+"F0.wireOp",EDGE,"E7.bottom")}),1.0]])]});
            var Q1;
            Q1=makeQuery(id+"F0.imprint","IMPRINT",FACE,{"disambiguationData":[TD([[makeQuery(id+"F0.imprint","IMPRINT",EDGE,{"derivedFrom":sQuery(id+"F0.wireOp",EDGE,"E7.bottom")}),-1.0]])]});
            var Q2;
            Q2=makeQuery(id+"F0.imprint","IMPRINT",FACE,{"disambiguationData":[TD([[makeQuery(id+"F0.imprint","IMPRINT",EDGE,{"derivedFrom":sQuery(id+"F0.wireOp",EDGE,"E8.bottom")}),1.0]])]});
            var Q3;
            Q3=makeQuery(id+"F0.imprint","IMPRINT",FACE,{"disambiguationData":[TD([[makeQuery(id+"F0.imprint","IMPRINT",EDGE,{"derivedFrom":sQuery(id+"F0.wireOp",EDGE,"E8.bottom")}),-1.0]])]});
            extrude(context, id + "F20", {"entities" : qUnion([Q0, Q1, Q2, Q3]), "operationType" : NewBodyOperationType.ADD, "depth" : 6.2 * mm});
        }
        {
            var Q0;
            Q0=makeQuery(id+"F0.imprint","IMPRINT",FACE,{"disambiguationData":[TD([[makeQuery(id+"F0.imprint","IMPRINT",EDGE,{"derivedFrom":sQuery(id+"F0.wireOp",EDGE,"E7.bottom")}),1.0]])]});
            var Q1;
            Q1=makeQuery(id+"F0.imprint","IMPRINT",FACE,{"disambiguationData":[TD([[makeQuery(id+"F0.imprint","IMPRINT",EDGE,{"derivedFrom":sQuery(id+"F0.wireOp",EDGE,"E8.bottom")}),1.0]])]});
            var Q2;
            Q2=makeQuery(id+"F0.imprint","IMPRINT",FACE,{"disambiguationData":[TD([[makeQuery(id+"F0.imprint","IMPRINT",EDGE,{"derivedFrom":sQuery(id+"F0.wireOp",EDGE,"E7.bottom")}),-1.0]])]});
            var Q3;
            Q3=makeQuery(id+"F0.imprint","IMPRINT",FACE,{"disambiguationData":[TD([[makeQuery(id+"F0.imprint","IMPRINT",EDGE,{"derivedFrom":sQuery(id+"F0.wireOp",EDGE,"E8.bottom")}),-1.0]])]});
            extrude(context, id + "F21", {"entities" : qUnion([Q0, Q1, Q2, Q3]), "operationType" : NewBodyOperationType.REMOVE, "depth" : 5.7 * mm});
        }
        {
            var Q0;
            Q0=makeQuery(id+"F1.opExtrude","SWEPT_FACE",FACE,{"disambiguationData":[OSD([sQuery(id+"F0.wireOp",EDGE,"E0.top"),sQuery(id+"F0.wireOp",EDGE,"E9.bottom"),sQuery(id+"F0.wireOp",EDGE,"E10.bottom")])]});
            var sketch = newSketch(context, id + "F22", { "sketchPlane" : qUnion([Q0])});
            skText(sketch, "E61", { "text": "5V", "fontName": "OpenSans-Bold.ttf"});
            skLineSegment(sketch, "E62.bottom", {"start": v(-9.26, 2.92) * mm, "end": v(-7.89, 2.92) * mm});
            skLineSegment(sketch, "E62.top", {"start": v(-9.26, 0.45) * mm, "end": v(-7.89, 0.45) * mm});
            skLineSegment(sketch, "E62.left", {"start": v(-9.46, 2.72) * mm, "end": v(-9.46, 0.65) * mm});
            skLineSegment(sketch, "E62.right", {"start": v(-7.69, 2.72) * mm, "end": v(-7.69, 0.65) * mm});
            skLineSegment(sketch, "E63.bottom", {"start": v(-8.88, 3.22) * mm, "end": v(-8.25, 3.22) * mm});
            skLineSegment(sketch, "E63.top", {"start": v(-9.08, 3.23) * mm, "end": v(-8.05, 3.23) * mm});
            skLineSegment(sketch, "E63.left", {"start": v(-9.08, 3.02) * mm, "end": v(-9.08, 2.92) * mm});
            skLineSegment(sketch, "E63.right", {"start": v(-8.05, 3.02) * mm, "end": v(-8.05, 2.92) * mm});
            skPoint(sketch, "E64.visualSharp", {"position": v(-9.46, 3.23) * mm});
            skArc(sketch, "E64.filletArc", {"start": v(-9.26, 2.92) * mm, "mid": v(-9.4, 2.86) * mm, "end": v(-9.46, 2.72) * mm});
            skPoint(sketch, "E65.visualSharp", {"position": v(-7.69, 3.23) * mm});
            skArc(sketch, "E65.filletArc", {"start": v(-7.69, 2.72) * mm, "mid": v(-7.75, 2.86) * mm, "end": v(-7.89, 2.92) * mm});
            skPoint(sketch, "E66.visualSharp", {"position": v(-9.46, 0.76) * mm});
            skArc(sketch, "E66.filletArc", {"start": v(-9.46, 0.65) * mm, "mid": v(-9.4, 0.5) * mm, "end": v(-9.26, 0.45) * mm});
            skPoint(sketch, "E67.visualSharp", {"position": v(-7.69, 0.76) * mm});
            skArc(sketch, "E67.filletArc", {"start": v(-7.89, 0.45) * mm, "mid": v(-7.75, 0.5) * mm, "end": v(-7.69, 0.65) * mm});
            skPoint(sketch, "E68.visualSharp", {"position": v(-9.08, 3.53) * mm});
            skArc(sketch, "E68.filletArc", {"start": v(-8.88, 3.22) * mm, "mid": v(-9.02, 3.16) * mm, "end": v(-9.08, 3.02) * mm});
            skPoint(sketch, "E69.visualSharp", {"position": v(-8.05, 3.53) * mm});
            skArc(sketch, "E69.filletArc", {"start": v(-8.05, 3.02) * mm, "mid": v(-8.1, 3.16) * mm, "end": v(-8.25, 3.22) * mm});
            skLineSegment(sketch, "E70.bottom", {"start": v(-9.11, 1.09) * mm, "end": v(-8, 1.09) * mm});
            skLineSegment(sketch, "E70.top", {"start": v(-9.11, 0.76) * mm, "end": v(-8, 0.76) * mm});
            skLineSegment(sketch, "E70.left", {"start": v(-9.11, 1.09) * mm, "end": v(-9.11, 0.76) * mm});
            skLineSegment(sketch, "E70.right", {"start": v(-8, 1.09) * mm, "end": v(-8, 0.76) * mm});
            skLineSegment(sketch, "E71.MirrorCS", {"start": v(-9.11, 1.41) * mm, "end": v(-8, 1.41) * mm});
            skLineSegment(sketch, "E72.bottom", {"start": v(-9.11, 1.74) * mm, "end": v(-8, 1.74) * mm});
            skLineSegment(sketch, "E72.top", {"start": v(-9.11, 1.73) * mm, "end": v(-8, 1.73) * mm});
            skLineSegment(sketch, "E72.left", {"start": v(-9.11, 1.74) * mm, "end": v(-9.11, 1.41) * mm});
            skLineSegment(sketch, "E72.right", {"start": v(-8, 1.74) * mm, "end": v(-8, 1.41) * mm});
            skLineSegment(sketch, "E73.MirrorCS", {"start": v(-9.11, 2.38) * mm, "end": v(-8, 2.38) * mm});
            skLineSegment(sketch, "E74.MirrorCS", {"start": v(-9.11, 2.06) * mm, "end": v(-8, 2.06) * mm});
            skLineSegment(sketch, "E75.bottom", {"start": v(-9.11, 2.4) * mm, "end": v(-8, 2.4) * mm});
            skLineSegment(sketch, "E75.left", {"start": v(-9.11, 2.4) * mm, "end": v(-9.11, 2.06) * mm});
            skLineSegment(sketch, "E75.right", {"start": v(-8, 2.4) * mm, "end": v(-8, 2.06) * mm});
            skLineSegment(sketch, "E76", {"start": v(-17.4, 3.32) * mm, "end": v(-16.81, 3.32) * mm});
            skLineSegment(sketch, "E77", {"start": v(-17.35, 2.16) * mm, "end": v(-16.59, 2.18) * mm});
            skLineSegment(sketch, "E78", {"start": v(-16.59, 2.18) * mm, "end": v(-18.15, 0.47) * mm});
            skLineSegment(sketch, "E79", {"start": v(-18.15, 0.47) * mm, "end": v(-17.5, 1.75) * mm});
            skLineSegment(sketch, "E80", {"start": v(-17.5, 1.75) * mm, "end": v(-18.15, 1.74) * mm});
            skLineSegment(sketch, "E81", {"start": v(-18.15, 1.74) * mm, "end": v(-17.4, 3.32) * mm});
            skLineSegment(sketch, "E82", {"start": v(-16.81, 3.32) * mm, "end": v(-17.35, 2.16) * mm});
            const initialGuessF22  = {"E61": [-0.03421, 0.0006, 1, 0, 0.0025]};
            skSetInitialGuess(sketch, initialGuessF22);
            skSolve(sketch);
        }
        {
            var Q0;
            Q0=qSketchRegion(id+"F22",true);
            extrude(context, id + "F23", {"entities" : qUnion([Q0]), "operationType" : NewBodyOperationType.REMOVE, "oppositeDirection" : true, "depth" : 0.2 * mm});
        }
        {
            var Q0;
            Q0=makeQuery(id+"F15.imprint","IMPRINT",FACE,{"disambiguationData":[TD([[makeQuery(id+"F15.imprint","IMPRINT",EDGE,{"derivedFrom":sQuery(id+"F15.wireOp",EDGE,"E40.sketch_text.stroke-29")}),-1.0]])]});
            var Q1;
            Q1=makeQuery(id+"F15.imprint","IMPRINT",FACE,{"disambiguationData":[TD([[makeQuery(id+"F15.imprint","IMPRINT",EDGE,{"derivedFrom":sQuery(id+"F15.wireOp",EDGE,"E40.sketch_text.stroke-48")}),-1.0]])]});
            var Q2;
            Q2=makeQuery(id+"F15.imprint","IMPRINT",FACE,{"disambiguationData":[TD([[makeQuery(id+"F15.imprint","IMPRINT",EDGE,{"derivedFrom":sQuery(id+"F15.wireOp",EDGE,"E40.sketch_text.stroke-15")}),-1.0]])]});
            var Q3;
            Q3=makeQuery(id+"F15.imprint","IMPRINT",FACE,{"disambiguationData":[TD([[makeQuery(id+"F15.imprint","IMPRINT",EDGE,{"derivedFrom":sQuery(id+"F15.wireOp",EDGE,"E40.sketch_text.stroke-0")}),-1.0]])]});
            extrude(context, id + "F24", {"entities" : qUnion([Q0, Q1, Q2, Q3]), "operationType" : NewBodyOperationType.REMOVE, "oppositeDirection" : true, "depth" : 0.2 * mm});
        }
        {
            var Q0;
            Q0=makeQuery(id+"F7.boolean.opBoolean","COPY",FACE,{"derivedFrom":makeQuery(id+"F7.opExtrude","CAP_FACE",FACE,{"disambiguationData":[OSD([sQuery(id+"F0.wireOp",EDGE,"E5.top"),sQuery(id+"F0.wireOp",EDGE,"E5.left"),sQuery(id+"F0.wireOp",EDGE,"E5.right"),sQuery(id+"F0.wireOp",EDGE,"E9.bottom"),sQuery(id+"F0.wireOp",EDGE,"E9.top"),sQuery(id+"F0.wireOp",EDGE,"E9.left"),sQuery(id+"F0.wireOp",EDGE,"E9.right")])],"isStart":false})});
            extrude(context, id + "F25", {"entities" : qUnion([Q0]), "operationType" : NewBodyOperationType.ADD, "depth" : 0.3 * mm});
        }
        {
            var Q0;
            Q0=makeQuery(id+"F25.opExtrude","CAP_FACE",FACE,{"disambiguationData":[OSD([sQuery(id+"F0.wireOp",EDGE,"E5.top"),sQuery(id+"F0.wireOp",EDGE,"E5.left"),sQuery(id+"F0.wireOp",EDGE,"E5.right"),sQuery(id+"F0.wireOp",EDGE,"E9.bottom"),sQuery(id+"F0.wireOp",EDGE,"E9.top"),sQuery(id+"F0.wireOp",EDGE,"E9.left"),sQuery(id+"F0.wireOp",EDGE,"E9.right")])],"isStart":false});
            var sketch = newSketch(context, id + "F26", { "sketchPlane" : qUnion([Q0])});
            skLineSegment(sketch, "E83.bottom", {"start": v(-29.5, 16.5) * mm, "end": v(-25.5, 16.5) * mm});
            skLineSegment(sketch, "E83.top", {"start": v(-29.5, 14.5) * mm, "end": v(-25.5, 14.5) * mm});
            skLineSegment(sketch, "E83.left", {"start": v(-29.5, 16.5) * mm, "end": v(-29.5, 14.5) * mm});
            skLineSegment(sketch, "E83.right", {"start": v(-25.5, 16.5) * mm, "end": v(-25.5, 14.5) * mm});
            skSolve(sketch);
        }
        {
            var Q0;
            Q0=makeQuery(id+"F26.imprint","IMPRINT",FACE,{"disambiguationData":[TD([[makeQuery(id+"F26.imprint","IMPRINT",EDGE,{"derivedFrom":sQuery(id+"F26.wireOp",EDGE,"E83.bottom")}),1.0]])]});
            extrude(context, id + "F27", {"entities" : qUnion([Q0]), "operationType" : NewBodyOperationType.ADD, "depth" : 3.7 * mm});
        }
        {
            var Q0;
            Q0=makeQuery(id+"F26.imprint","IMPRINT",FACE,{"disambiguationData":[TD([[makeQuery(id+"F26.imprint","IMPRINT",EDGE,{"derivedFrom":sQuery(id+"F26.wireOp",EDGE,"E83.bottom")}),1.0]])]});
            extrude(context, id + "F28", {"entities" : qUnion([Q0]), "operationType" : NewBodyOperationType.REMOVE, "depth" : 3.4 * mm});
        }
        {
            var Q0;
            Q0=makeQuery(id+"F7.boolean.opBoolean","COPY",FACE,{"derivedFrom":makeQuery(id+"F7.opExtrude","CAP_FACE",FACE,{"disambiguationData":[OSD([sQuery(id+"F0.wireOp",EDGE,"E0.top"),sQuery(id+"F0.wireOp",EDGE,"E6.top"),sQuery(id+"F0.wireOp",EDGE,"E6.left"),sQuery(id+"F0.wireOp",EDGE,"E6.right"),sQuery(id+"F0.wireOp",EDGE,"E10.bottom"),sQuery(id+"F0.wireOp",EDGE,"E10.top"),sQuery(id+"F0.wireOp",EDGE,"E10.left"),sQuery(id+"F0.wireOp",EDGE,"E10.right")])],"isStart":false})});
            extrude(context, id + "F29", {"entities" : qUnion([Q0]), "operationType" : NewBodyOperationType.ADD, "depth" : 0.3 * mm});
        }
        {
            var Q0;
            Q0=makeQuery(id+"F29.opExtrude","CAP_FACE",FACE,{"disambiguationData":[OSD([sQuery(id+"F0.wireOp",EDGE,"E0.top"),sQuery(id+"F0.wireOp",EDGE,"E6.top"),sQuery(id+"F0.wireOp",EDGE,"E6.left"),sQuery(id+"F0.wireOp",EDGE,"E6.right"),sQuery(id+"F0.wireOp",EDGE,"E10.bottom"),sQuery(id+"F0.wireOp",EDGE,"E10.top"),sQuery(id+"F0.wireOp",EDGE,"E10.left"),sQuery(id+"F0.wireOp",EDGE,"E10.right")])],"isStart":false});
            var sketch = newSketch(context, id + "F30", { "sketchPlane" : qUnion([Q0])});
            skLineSegment(sketch, "E84.bottom", {"start": v(-15.5, 14.5) * mm, "end": v(-10, 14.5) * mm});
            skLineSegment(sketch, "E84.top", {"start": v(-15.5, 16.5) * mm, "end": v(-10, 16.5) * mm});
            skLineSegment(sketch, "E84.left", {"start": v(-15.5, 14.5) * mm, "end": v(-15.5, 16.5) * mm});
            skLineSegment(sketch, "E84.right", {"start": v(-10, 14.5) * mm, "end": v(-10, 16.5) * mm});
            skSolve(sketch);
        }
        {
            var Q0;
            Q0=makeQuery(id+"F30.imprint","IMPRINT",FACE,{"disambiguationData":[TD([[makeQuery(id+"F30.imprint","IMPRINT",EDGE,{"derivedFrom":sQuery(id+"F30.wireOp",EDGE,"E84.bottom")}),-1.0]])]});
            extrude(context, id + "F31", {"entities" : qUnion([Q0]), "operationType" : NewBodyOperationType.ADD, "depth" : 3.7 * mm});
        }
        {
            var Q0;
            Q0=makeQuery(id+"F30.imprint","IMPRINT",FACE,{"disambiguationData":[TD([[makeQuery(id+"F30.imprint","IMPRINT",EDGE,{"derivedFrom":sQuery(id+"F30.wireOp",EDGE,"E84.bottom")}),-1.0]])]});
            extrude(context, id + "F32", {"entities" : qUnion([Q0]), "operationType" : NewBodyOperationType.REMOVE, "depth" : 3.4 * mm});
        }
        {
            var Q0;
            {var subQ1=sQuery(id+"F0.wireOp",EDGE,"E1.bottom");var subQ3=sQuery(id+"F0.wireOp",EDGE,"E11.bottom");var subQ4=sQuery(id+"F0.wireOp",EDGE,"E1.top");var subQ5=sQuery(id+"F0.wireOp",EDGE,"E1.right");var subQ6=makeQuery(id+"F2.opExtrude","SWEPT_FACE",FACE,{"disambiguationData":[OSD([subQ5])]});var subQ8=sQuery(id+"F0.wireOp",EDGE,"E11.top");var subQ14=sQuery(id+"F0.wireOp",EDGE,"E3");var subQ15=sQuery(id+"F0.wireOp",EDGE,"E1.left");var subQ16=sQuery(id+"F0.wireOp",EDGE,"E4");var subQ17=sQuery(id+"F0.wireOp",EDGE,"E2");Q0=makeQuery(id+"F14.boolean.opBoolean","SPLIT",FACE,{"disambiguationData":[TD([subQ6])],"derivedFrom":makeQuery(id+"F11.boolean.opBoolean","SPLIT",FACE,{"disambiguationData":[TD([subQ6])],"derivedFrom":makeQuery(id+"F9.boolean.opBoolean","MERGE",FACE,{"derivedFrom":[makeQuery(id+"F5.opShell","OFFSET_FACE",FACE,{"disambiguationData":[OSD([sQuery(id+"F0.wireOp",EDGE,"E0.bottom"),sQuery(id+"F0.wireOp",EDGE,"E0.top"),sQuery(id+"F0.wireOp",EDGE,"E0.right"),subQ1,subQ4,subQ15,subQ5,subQ17,subQ14,subQ16,sQuery(id+"F0.wireOp",EDGE,"E9.bottom"),sQuery(id+"F0.wireOp",EDGE,"E9.top"),sQuery(id+"F0.wireOp",EDGE,"E9.left"),sQuery(id+"F0.wireOp",EDGE,"E9.right"),sQuery(id+"F0.wireOp",EDGE,"E10.bottom"),sQuery(id+"F0.wireOp",EDGE,"E10.top"),sQuery(id+"F0.wireOp",EDGE,"E10.left"),sQuery(id+"F0.wireOp",EDGE,"E10.right"),subQ3,subQ8,sQuery(id+"F0.wireOp",EDGE,"E17.0"),sQuery(id+"F0.wireOp",EDGE,"E17.1"),sQuery(id+"F0.wireOp",EDGE,"E17.2"),sQuery(id+"F0.wireOp",EDGE,"E17.3"),sQuery(id+"F0.wireOp",EDGE,"E18.0"),sQuery(id+"F0.wireOp",EDGE,"E18.1"),sQuery(id+"F0.wireOp",EDGE,"E18.2"),sQuery(id+"F0.wireOp",EDGE,"E18.3")])]}),makeQuery(id+"F9.opExtrude","SWEPT_FACE",FACE,{"disambiguationData":[OSD([subQ5]),TDD([makeQuery(id+"F5.opShell","OFFSET_EDGE",EDGE,{"disambiguationData":[OSD([subQ5]),TDD([makeQuery(id+"F2.opExtrude","CAP_EDGE",EDGE,{"disambiguationData":[OSD([subQ5])],"isStart":false})])]})])]})]})})});}
            var Q1;
            {var subQ1=sQuery(id+"F0.wireOp",EDGE,"E1.top");var subQ3=sQuery(id+"F0.wireOp",EDGE,"E11.top");var subQ4=sQuery(id+"F0.wireOp",EDGE,"E1.bottom");var subQ7=sQuery(id+"F0.wireOp",EDGE,"E14");var subQ8=sQuery(id+"F0.wireOp",EDGE,"E11.bottom");var subQ10=sQuery(id+"F0.wireOp",EDGE,"E1.right");var subQ13=sQuery(id+"F0.wireOp",EDGE,"E3");var subQ14=sQuery(id+"F0.wireOp",EDGE,"E1.left");var subQ15=sQuery(id+"F0.wireOp",EDGE,"E4");var subQ16=sQuery(id+"F0.wireOp",EDGE,"E2");Q1=makeQuery(id+"F14.boolean.opBoolean","SPLIT",FACE,{"disambiguationData":[TD([makeQuery(id+"F14.opExtrude","SWEPT_FACE",FACE,{"disambiguationData":[OSD([subQ7])]})])],"derivedFrom":makeQuery(id+"F11.boolean.opBoolean","SPLIT",FACE,{"disambiguationData":[TD([makeQuery(id+"F2.opExtrude","SWEPT_FACE",FACE,{"disambiguationData":[OSD([subQ10])]})])],"derivedFrom":makeQuery(id+"F9.boolean.opBoolean","MERGE",FACE,{"derivedFrom":[makeQuery(id+"F5.opShell","OFFSET_FACE",FACE,{"disambiguationData":[OSD([sQuery(id+"F0.wireOp",EDGE,"E0.bottom"),sQuery(id+"F0.wireOp",EDGE,"E0.top"),sQuery(id+"F0.wireOp",EDGE,"E0.right"),subQ4,subQ1,subQ14,subQ10,subQ16,subQ13,subQ15,sQuery(id+"F0.wireOp",EDGE,"E9.bottom"),sQuery(id+"F0.wireOp",EDGE,"E9.top"),sQuery(id+"F0.wireOp",EDGE,"E9.left"),sQuery(id+"F0.wireOp",EDGE,"E9.right"),sQuery(id+"F0.wireOp",EDGE,"E10.bottom"),sQuery(id+"F0.wireOp",EDGE,"E10.top"),sQuery(id+"F0.wireOp",EDGE,"E10.left"),sQuery(id+"F0.wireOp",EDGE,"E10.right"),subQ8,subQ3,sQuery(id+"F0.wireOp",EDGE,"E17.0"),sQuery(id+"F0.wireOp",EDGE,"E17.1"),sQuery(id+"F0.wireOp",EDGE,"E17.2"),sQuery(id+"F0.wireOp",EDGE,"E17.3"),sQuery(id+"F0.wireOp",EDGE,"E18.0"),sQuery(id+"F0.wireOp",EDGE,"E18.1"),sQuery(id+"F0.wireOp",EDGE,"E18.2"),sQuery(id+"F0.wireOp",EDGE,"E18.3")])]}),makeQuery(id+"F9.opExtrude","SWEPT_FACE",FACE,{"disambiguationData":[OSD([subQ10]),TDD([makeQuery(id+"F5.opShell","OFFSET_EDGE",EDGE,{"disambiguationData":[OSD([subQ10]),TDD([makeQuery(id+"F2.opExtrude","CAP_EDGE",EDGE,{"disambiguationData":[OSD([subQ10])],"isStart":false})])]})])]})]})})});}
            extrude(context, id + "F33", {"entities" : qUnion([Q0, Q1]), "operationType" : NewBodyOperationType.ADD, "depth" : 0.5 * mm});
        }
        {
            var Q0;
            Q0=makeQuery(id+"F14.boolean.opBoolean","COPY",FACE,{"derivedFrom":makeQuery(id+"F14.opExtrude","CAP_FACE",FACE,{"disambiguationData":[OSD([sQuery(id+"F0.wireOp",EDGE,"E1.bottom"),sQuery(id+"F0.wireOp",EDGE,"E1.top"),sQuery(id+"F0.wireOp",EDGE,"E15"),sQuery(id+"F0.wireOp",EDGE,"E16")])],"isStart":false})});
            extrude(context, id + "F34", {"entities" : qUnion([Q0]), "operationType" : NewBodyOperationType.REMOVE, "oppositeDirection" : true, "depth" : 0.3 * mm});
        }
        {
            var Q0;
            {var subQ0=sQuery(id+"F0.wireOp",EDGE,"E3");var subQ1=sQuery(id+"F0.wireOp",EDGE,"E2");var subQ2=sQuery(id+"F0.wireOp",EDGE,"E0.right");var subQ3=sQuery(id+"F0.wireOp",EDGE,"E0.bottom");var subQ4=sQuery(id+"F0.wireOp",EDGE,"E10.bottom");var subQ5=sQuery(id+"F0.wireOp",EDGE,"E9.bottom");var subQ6=sQuery(id+"F0.wireOp",EDGE,"E0.top");var subQ7=sQuery(id+"F0.wireOp",EDGE,"E1.right");Q0=makeQuery(id+"F11.boolean.opBoolean","SPLIT",FACE,{"disambiguationData":[TD([makeQuery(id+"F5.opShell","OFFSET_FACE",FACE,{"disambiguationData":[OSD([subQ3])]})])],"derivedFrom":makeQuery(id+"F9.boolean.opBoolean","MERGE",FACE,{"derivedFrom":[makeQuery(id+"F5.opShell","OFFSET_FACE",FACE,{"disambiguationData":[OSD([subQ3,subQ6,subQ2,sQuery(id+"F0.wireOp",EDGE,"E1.bottom"),sQuery(id+"F0.wireOp",EDGE,"E1.top"),sQuery(id+"F0.wireOp",EDGE,"E1.left"),subQ7,subQ1,subQ0,sQuery(id+"F0.wireOp",EDGE,"E4"),subQ5,sQuery(id+"F0.wireOp",EDGE,"E9.top"),sQuery(id+"F0.wireOp",EDGE,"E9.left"),sQuery(id+"F0.wireOp",EDGE,"E9.right"),subQ4,sQuery(id+"F0.wireOp",EDGE,"E10.top"),sQuery(id+"F0.wireOp",EDGE,"E10.left"),sQuery(id+"F0.wireOp",EDGE,"E10.right"),sQuery(id+"F0.wireOp",EDGE,"E11.bottom"),sQuery(id+"F0.wireOp",EDGE,"E11.top"),sQuery(id+"F0.wireOp",EDGE,"E17.0"),sQuery(id+"F0.wireOp",EDGE,"E17.1"),sQuery(id+"F0.wireOp",EDGE,"E17.2"),sQuery(id+"F0.wireOp",EDGE,"E17.3"),sQuery(id+"F0.wireOp",EDGE,"E18.0"),sQuery(id+"F0.wireOp",EDGE,"E18.1"),sQuery(id+"F0.wireOp",EDGE,"E18.2"),sQuery(id+"F0.wireOp",EDGE,"E18.3")])]}),makeQuery(id+"F9.opExtrude","SWEPT_FACE",FACE,{"disambiguationData":[OSD([subQ7]),TDD([makeQuery(id+"F5.opShell","OFFSET_EDGE",EDGE,{"disambiguationData":[OSD([subQ7]),TDD([makeQuery(id+"F2.opExtrude","CAP_EDGE",EDGE,{"disambiguationData":[OSD([subQ7])],"isStart":false})])]})])]})]})});}
            var sketch = newSketch(context, id + "F35", { "sketchPlane" : qUnion([Q0])});
            skLineSegment(sketch, "E85.bottom", {"start": v(-30.25, 14.5) * mm, "end": v(0, 14.5) * mm});
            skLineSegment(sketch, "E85.top", {"start": v(-30.25, 2.33) * mm, "end": v(0, 2.33) * mm});
            skLineSegment(sketch, "E85.left", {"start": v(-30.25, 14.5) * mm, "end": v(-30.25, 2.33) * mm});
            skLineSegment(sketch, "E85.right", {"start": v(0, 14.5) * mm, "end": v(0, 2.33) * mm});
            skLineSegment(sketch, "E86.bottom", {"start": v(-18.2, 7.5) * mm, "end": v(-22.2, 7.5) * mm});
            skLineSegment(sketch, "E86.top", {"start": v(-18.2, 13) * mm, "end": v(-22.2, 13) * mm});
            skLineSegment(sketch, "E86.left", {"start": v(-18.2, 7.5) * mm, "end": v(-18.2, 13) * mm});
            skLineSegment(sketch, "E86.right", {"start": v(-22.2, 7.5) * mm, "end": v(-22.2, 13) * mm});
            skPoint(sketch, "E86.middle", {"position": v(-20.2, 10.25) * mm});
            skPoint(sketch, "E86.middle.positionSnap0", {"position": v(-18.7, 10.25) * mm});
            skPoint(sketch, "E86.centerSnap0", {"position": v(-18.7, 10.25) * mm});
            skLineSegment(sketch, "E87.bottom", {"start": v(-5.5, 7.5) * mm, "end": v(-9.5, 7.5) * mm});
            skLineSegment(sketch, "E87.top", {"start": v(-5.5, 13) * mm, "end": v(-9.5, 13) * mm});
            skLineSegment(sketch, "E87.left", {"start": v(-5.5, 7.5) * mm, "end": v(-5.5, 13) * mm});
            skLineSegment(sketch, "E87.right", {"start": v(-9.5, 7.5) * mm, "end": v(-9.5, 13) * mm});
            skPoint(sketch, "E87.middle", {"position": v(-7.5, 10.25) * mm});
            skSolve(sketch);
        }
        {
            var Q0;
            Q0=makeQuery(id+"F35.imprint","IMPRINT",FACE,{"disambiguationData":[TD([[makeQuery(id+"F35.imprint","IMPRINT",EDGE,{"derivedFrom":sQuery(id+"F35.wireOp",EDGE,"E85.bottom")}),1.0]])]});
            extrude(context, id + "F36", {"entities" : qUnion([Q0]), "operationType" : NewBodyOperationType.ADD, "depth" : 0.8 * mm});
        }
        {
            var Q0;
            Q0=makeQuery(id+"F36.opExtrude","CAP_EDGE",EDGE,{"disambiguationData":[OSD([sQuery(id+"F35.wireOp",EDGE,"E85.left")])],"isStart":false});
            var Q1;
            Q1=makeQuery(id+"F36.opExtrude","CAP_EDGE",EDGE,{"disambiguationData":[OSD([sQuery(id+"F35.wireOp",EDGE,"E85.right")])],"isStart":false});
            chamfer(context, id + "F37", {"entities" : qUnion([Q0, Q1]), "width" : 0.8 * mm, "tangentPropagation" : true});
        }
        {
            var Q0;
            Q0=makeQuery(id+"F5.opShell","OFFSET_FACE",FACE,{"disambiguationData":[OSD([sQuery(id+"F0.wireOp",EDGE,"E0.bottom")])]});
            var sketch = newSketch(context, id + "F38", { "sketchPlane" : qUnion([Q0])});
            skLineSegment(sketch, "E88.bottom", {"start": v(-36, 0) * mm, "end": v(-33, 0) * mm});
            skLineSegment(sketch, "E88.top", {"start": v(-36, 2) * mm, "end": v(-33, 2) * mm});
            skLineSegment(sketch, "E88.left", {"start": v(-36, 0) * mm, "end": v(-36, 2) * mm});
            skLineSegment(sketch, "E88.right", {"start": v(-33, 0) * mm, "end": v(-33, 2) * mm});
            skLineSegment(sketch, "E89.1.0.0", {"start": v(-21, 0) * mm, "end": v(-18, 0) * mm});
            skLineSegment(sketch, "E89.1.0.1", {"start": v(-21, 2) * mm, "end": v(-18, 2) * mm});
            skLineSegment(sketch, "E89.1.0.2", {"start": v(-18, 0) * mm, "end": v(-18, 2) * mm});
            skLineSegment(sketch, "E89.1.0.3", {"start": v(-21, 0) * mm, "end": v(-21, 2) * mm});
            skLineSegment(sketch, "E89.2.0.0", {"start": v(-6, 0) * mm, "end": v(-3, 0) * mm});
            skLineSegment(sketch, "E89.2.0.1", {"start": v(-6, 2) * mm, "end": v(-3, 2) * mm});
            skLineSegment(sketch, "E89.2.0.2", {"start": v(-3, 0) * mm, "end": v(-3, 2) * mm});
            skLineSegment(sketch, "E89.2.0.3", {"start": v(-6, 0) * mm, "end": v(-6, 2) * mm});
            skLineSegment(sketch, "E89.direction1", {"start": v(-37, 0) * mm, "end": v(-22, 0) * mm, "construction": true});
            skSolve(sketch);
        }
        {
            var Q0;
            Q0=makeQuery(id+"F38.imprint","IMPRINT",FACE,{"disambiguationData":[TD([[makeQuery(id+"F38.imprint","IMPRINT",EDGE,{"derivedFrom":sQuery(id+"F38.wireOp",EDGE,"E88.bottom")}),-1.0]])]});
            var Q1;
            Q1=makeQuery(id+"F38.imprint","IMPRINT",FACE,{"disambiguationData":[TD([[makeQuery(id+"F38.imprint","IMPRINT",EDGE,{"derivedFrom":sQuery(id+"F38.wireOp",EDGE,"E89.1.0.0")}),-1.0]])]});
            var Q2;
            Q2=makeQuery(id+"F38.imprint","IMPRINT",FACE,{"disambiguationData":[TD([[makeQuery(id+"F38.imprint","IMPRINT",EDGE,{"derivedFrom":sQuery(id+"F38.wireOp",EDGE,"E89.2.0.0")}),-1.0]])]});
            extrude(context, id + "F39", {"entities" : qUnion([Q0, Q1, Q2]), "operationType" : NewBodyOperationType.ADD, "endBound" : BoundingType.UP_TO_NEXT, "depth" : 25 * mm});
        }
        {
            var Q0;
            {var subQ0=sQuery(id+"F0.wireOp",EDGE,"E1.top");var subQ1=sQuery(id+"F0.wireOp",EDGE,"E11.bottom");Q0=makeQuery(id+"F34.boolean.opBoolean","MERGE",FACE,{"derivedFrom":[makeQuery(id+"F14.boolean.opBoolean","MERGE",FACE,{"derivedFrom":[makeQuery(id+"F12.boolean.opBoolean","MERGE",FACE,{"derivedFrom":[makeQuery(id+"F9.boolean.opBoolean","MERGE",FACE,{"derivedFrom":[makeQuery(id+"F5.opShell","OFFSET_FACE",FACE,{"disambiguationData":[OSD([subQ0,subQ1])]}),makeQuery(id+"F9.opExtrude","SWEPT_FACE",FACE,{"disambiguationData":[OSD([subQ0,sQuery(id+"F0.wireOp",EDGE,"E1.right")])]})]}),makeQuery(id+"F12.opExtrude","SWEPT_FACE",FACE,{"disambiguationData":[OSD([subQ0,subQ1])]})]}),makeQuery(id+"F14.opExtrude","SWEPT_FACE",FACE,{"disambiguationData":[OSD([subQ0]),TDD([makeQuery(id+"F0.imprint","IMPRINT",EDGE,{"disambiguationData":[TD([[makeQuery(id+"F0.imprint","INTERSECT",VERTEX,{"derivedFrom":[subQ0,sQuery(id+"F0.wireOp",EDGE,"E14")]}),1.0]])],"derivedFrom":subQ0})])]}),makeQuery(id+"F14.opExtrude","SWEPT_FACE",FACE,{"disambiguationData":[OSD([subQ0]),TDD([makeQuery(id+"F0.imprint","IMPRINT",EDGE,{"disambiguationData":[TD([[makeQuery(id+"F0.imprint","INTERSECT",VERTEX,{"derivedFrom":[subQ0,sQuery(id+"F0.wireOp",EDGE,"E15")]}),1.0]])],"derivedFrom":subQ0})])]})]}),makeQuery(id+"F34.opExtrude","SWEPT_FACE",FACE,{"disambiguationData":[OSD([subQ0])]})]});}
            var sketch = newSketch(context, id + "F40", { "sketchPlane" : qUnion([Q0])});
            skLineSegment(sketch, "E90.bottom", {"start": v(-6, 0) * mm, "end": v(-8, 0) * mm});
            skLineSegment(sketch, "E90.top", {"start": v(-6, 2) * mm, "end": v(-8, 2) * mm});
            skLineSegment(sketch, "E90.left", {"start": v(-6, 0) * mm, "end": v(-6, 2) * mm});
            skLineSegment(sketch, "E90.right", {"start": v(-8, 0) * mm, "end": v(-8, 2) * mm});
            skLineSegment(sketch, "E91.1.0.0", {"start": v(-19, 0) * mm, "end": v(-21, 0) * mm});
            skLineSegment(sketch, "E91.1.0.1", {"start": v(-19, 0) * mm, "end": v(-19, 2) * mm});
            skLineSegment(sketch, "E91.1.0.2", {"start": v(-21, 0) * mm, "end": v(-21, 2) * mm});
            skLineSegment(sketch, "E91.1.0.3", {"start": v(-19, 2) * mm, "end": v(-21, 2) * mm});
            skLineSegment(sketch, "E91.2.0.0", {"start": v(-32, 0) * mm, "end": v(-34, 0) * mm});
            skLineSegment(sketch, "E91.2.0.1", {"start": v(-32, 0) * mm, "end": v(-32, 2) * mm});
            skLineSegment(sketch, "E91.2.0.2", {"start": v(-34, 0) * mm, "end": v(-34, 2) * mm});
            skLineSegment(sketch, "E91.2.0.3", {"start": v(-32, 2) * mm, "end": v(-34, 2) * mm});
            skLineSegment(sketch, "E91.direction1", {"start": v(-8, 0) * mm, "end": v(-21, 0) * mm, "construction": true});
            skSolve(sketch);
        }
        {
            var Q0;
            Q0=makeQuery(id+"F40.imprint","IMPRINT",FACE,{"disambiguationData":[TD([[makeQuery(id+"F40.imprint","IMPRINT",EDGE,{"derivedFrom":sQuery(id+"F40.wireOp",EDGE,"E90.bottom")}),-1.0]])]});
            var Q1;
            Q1=makeQuery(id+"F40.imprint","IMPRINT",FACE,{"disambiguationData":[TD([[makeQuery(id+"F40.imprint","IMPRINT",EDGE,{"derivedFrom":sQuery(id+"F40.wireOp",EDGE,"E91.1.0.0")}),-1.0]])]});
            var Q2;
            Q2=makeQuery(id+"F40.imprint","IMPRINT",FACE,{"disambiguationData":[TD([[makeQuery(id+"F40.imprint","IMPRINT",EDGE,{"derivedFrom":sQuery(id+"F40.wireOp",EDGE,"E91.2.0.0")}),-1.0]])]});
            var Q3;
            Q3=makeQuery(id+"F40.imprint","IMPRINT",FACE,{"disambiguationData":[TD([[makeQuery(id+"F40.imprint","IMPRINT",EDGE,{"derivedFrom":sQuery(id+"F40.wireOp",EDGE,"E91.3.0.0")}),-1.0]])]});
            var Q4;
            Q4=makeQuery(id+"F40.imprint","IMPRINT",FACE,{"disambiguationData":[TD([[makeQuery(id+"F40.imprint","IMPRINT",EDGE,{"derivedFrom":sQuery(id+"F40.wireOp",EDGE,"E91.4.0.0")}),-1.0]])]});
            extrude(context, id + "F41", {"entities" : qUnion([Q0, Q1, Q2, Q3, Q4]), "operationType" : NewBodyOperationType.ADD, "endBound" : BoundingType.UP_TO_NEXT, "depth" : 25 * mm});
        }
        {
            var Q0;
            Q0=makeQuery(id+"F1.opExtrude","SWEPT_FACE",FACE,{"disambiguationData":[OSD([sQuery(id+"F0.wireOp",EDGE,"E0.right")])]});
            var sketch = newSketch(context, id + "F42", { "sketchPlane" : qUnion([Q0])});
            skLineSegment(sketch, "E92.bottom", {"start": v(26.5, 16.5) * mm, "end": v(-26.5, 16.5) * mm});
            skLineSegment(sketch, "E92.top", {"start": v(26.5, -10) * mm, "end": v(-26.5, -10) * mm});
            skLineSegment(sketch, "E92.left", {"start": v(26.5, 16.5) * mm, "end": v(26.5, -10) * mm});
            skLineSegment(sketch, "E92.right", {"start": v(-26.5, 16.5) * mm, "end": v(-26.5, -10) * mm});
            skPoint(sketch, "E92.middle", {"position": v(0, 36.07) * mm});
            skSolve(sketch);
        }
        {
            var Q0;
            Q0=makeQuery(id+"F42.imprint","IMPRINT",FACE,{"disambiguationData":[TD([[makeQuery(id+"F42.imprint","IMPRINT",EDGE,{"derivedFrom":sQuery(id+"F42.wireOp",EDGE,"E92.bottom")}),1.0]])]});
            extrude(context, id + "F43", {"entities" : qUnion([Q0]), "operationType" : NewBodyOperationType.ADD, "oppositeDirection" : true, "depth" : 0.2 * mm});
        }
    });
